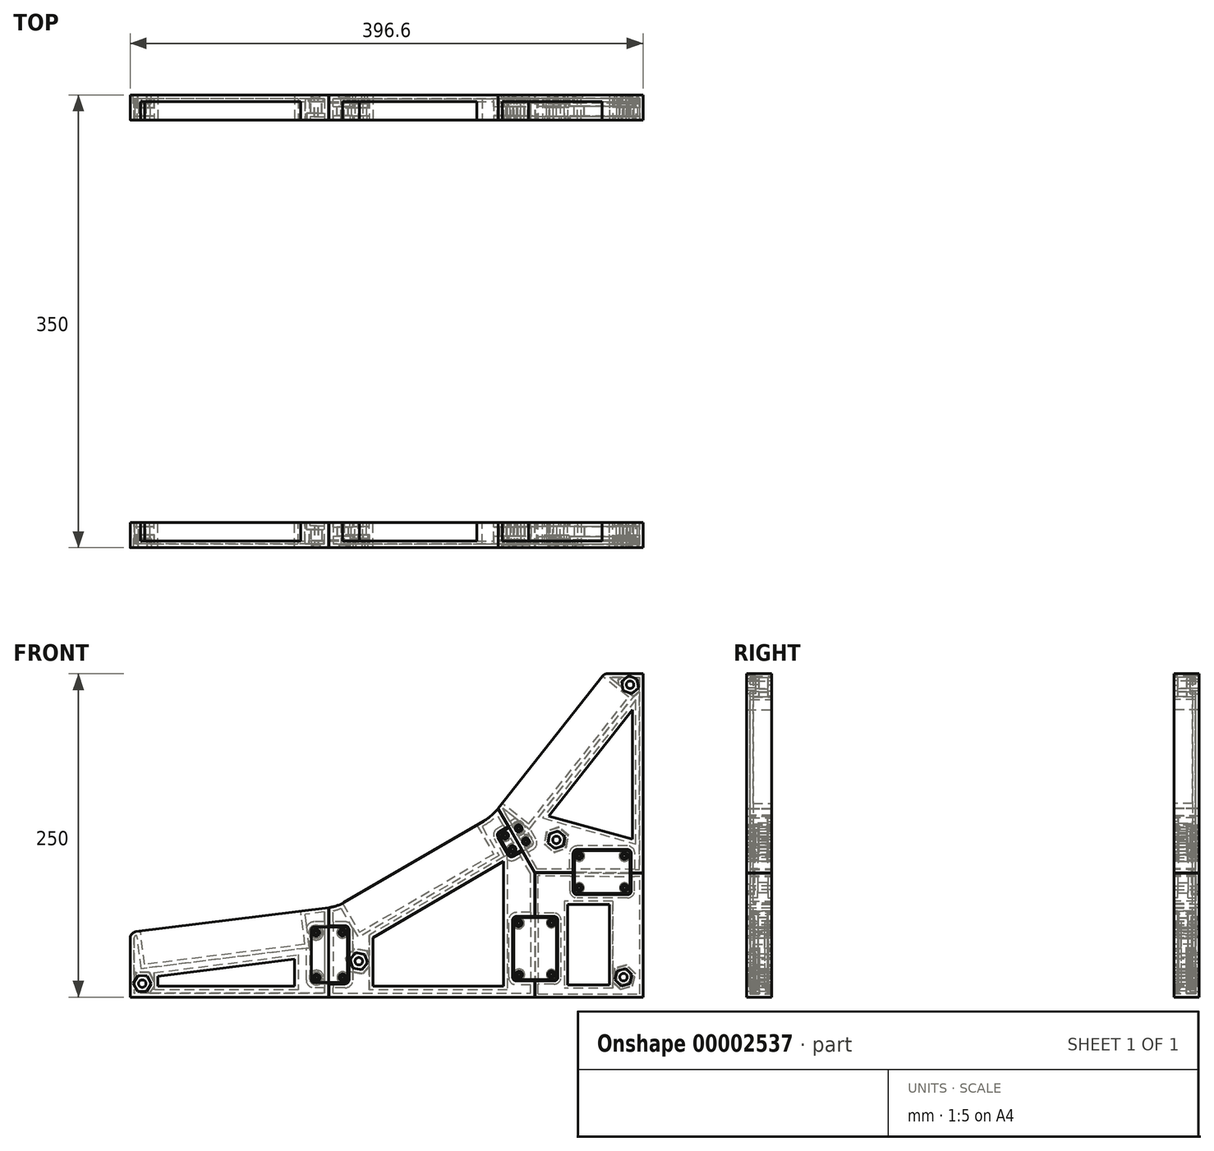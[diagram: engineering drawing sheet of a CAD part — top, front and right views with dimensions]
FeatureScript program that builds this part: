
annotation { "Feature Type Name" : "Feature", "Feature Type Description" : "" }
export const myFeature = defineFeature(function(context is Context, id is Id, definition is map)
    precondition{}
    {
        {
            var Q0;
            Q0=qCreatedBy(makeId("Front.planeOp"),FACE);
            var sketch = newSketch(context, id + "F0", { "sketchPlane" : qUnion([Q0])});
            skLineSegment(sketch, "E0", {"start": v(-139.2, -96.22) * mm, "end": v(-139.2, -46.22) * mm});
            skLineSegment(sketch, "E1", {"start": v(-139.2, -46.22) * mm, "end": v(20.8, -26.22) * mm});
            skLineSegment(sketch, "E2", {"start": v(20.8, -26.22) * mm, "end": v(140.8, 43.78) * mm});
            skLineSegment(sketch, "E3", {"start": v(140.8, 43.78) * mm, "end": v(227.4, 153.78) * mm});
            skLineSegment(sketch, "E4", {"start": v(227.4, 153.78) * mm, "end": v(257.4, 153.78) * mm});
            skLineSegment(sketch, "E5", {"start": v(257.4, 153.78) * mm, "end": v(257.4, -96.22) * mm});
            skLineSegment(sketch, "E6", {"start": v(257.4, -96.22) * mm, "end": v(-139.2, -96.22) * mm});
            skLineSegment(sketch, "E7", {"start": v(20.8, -26.22) * mm, "end": v(20.8, -96.22) * mm});
            skLineSegment(sketch, "E8", {"start": v(140.8, 43.78) * mm, "end": v(140.8, -96.22) * mm});
            skSolve(sketch);
        }
        {
            var Q0;
            {var subQ2=sQuery(id+"F0.wireOp",EDGE,"E0");Q0=makeQuery(id+"F0.imprint","IMPRINT",FACE,{"disambiguationData":[TD([[makeQuery(id+"F0.imprint","IMPRINT",EDGE,{"derivedFrom":subQ2}),-1.0]])]});}
            var Q1;
            Q1=makeQuery(id+"F0.imprint","IMPRINT",FACE,{"disambiguationData":[TD([[makeQuery(id+"F0.imprint","IMPRINT",EDGE,{"derivedFrom":sQuery(id+"F0.wireOp",EDGE,"E2")}),-1.0]])]});
            var Q2;
            Q2=makeQuery(id+"F0.imprint","IMPRINT",FACE,{"disambiguationData":[TD([[makeQuery(id+"F0.imprint","IMPRINT",EDGE,{"derivedFrom":sQuery(id+"F0.wireOp",EDGE,"E3")}),-1.0]])]});
            extrude(context, id + "F1", {"entities" : qUnion([Q0, Q1, Q2]), "oppositeDirection" : true, "depth" : 25 * mm});
        }
        {
            var Q0;
            Q0=makeQuery(id+"F1.opExtrude","CAP_FACE",FACE,{"disambiguationData":[OSD([sQuery(id+"F0.wireOp",EDGE,"E0"),sQuery(id+"F0.wireOp",EDGE,"E1"),sQuery(id+"F0.wireOp",EDGE,"E2"),sQuery(id+"F0.wireOp",EDGE,"E3"),sQuery(id+"F0.wireOp",EDGE,"E4"),sQuery(id+"F0.wireOp",EDGE,"E5"),sQuery(id+"F0.wireOp",EDGE,"E6")])],"isStart":true});
            var sketch = newSketch(context, id + "F2", { "sketchPlane" : qUnion([Q0])});
            skLineSegment(sketch, "E9.bottom", {"start": v(-131.26, -45.23) * mm, "end": v(-7.23, -29.73) * mm});
            skLineSegment(sketch, "E9.top", {"start": v(-128.04, -71.03) * mm, "end": v(-4, -55.53) * mm});
            skLineSegment(sketch, "E9.left", {"start": v(-131.26, -45.23) * mm, "end": v(-128.04, -71.03) * mm});
            skLineSegment(sketch, "E9.right", {"start": v(-7.23, -29.73) * mm, "end": v(-4, -55.53) * mm});
            skLineSegment(sketch, "E10.bottom", {"start": v(38.22, -46.16) * mm, "end": v(141.87, 14.3) * mm});
            skLineSegment(sketch, "E10.top", {"start": v(25.12, -23.7) * mm, "end": v(128.77, 36.76) * mm});
            skLineSegment(sketch, "E10.left", {"start": v(38.22, -46.16) * mm, "end": v(25.12, -23.7) * mm});
            skLineSegment(sketch, "E10.right", {"start": v(141.87, 14.3) * mm, "end": v(128.77, 36.76) * mm});
            skLineSegment(sketch, "E11.bottom", {"start": v(225.85, 151.81) * mm, "end": v(148.53, 53.6) * mm});
            skLineSegment(sketch, "E11.top", {"start": v(246.28, 135.73) * mm, "end": v(168.96, 37.51) * mm});
            skLineSegment(sketch, "E11.left", {"start": v(225.85, 151.81) * mm, "end": v(246.28, 135.73) * mm});
            skLineSegment(sketch, "E11.right", {"start": v(148.53, 53.6) * mm, "end": v(168.96, 37.51) * mm});
            skSolve(sketch);
        }
        {
            var Q0;
            Q0=makeQuery(id+"F2.imprint","IMPRINT",FACE,{"disambiguationData":[TD([[makeQuery(id+"F2.imprint","IMPRINT",EDGE,{"derivedFrom":sQuery(id+"F2.wireOp",EDGE,"E9.bottom")}),-1.0]])]});
            var Q1;
            Q1=makeQuery(id+"F2.imprint","IMPRINT",FACE,{"disambiguationData":[TD([[makeQuery(id+"F2.imprint","IMPRINT",EDGE,{"derivedFrom":sQuery(id+"F2.wireOp",EDGE,"E10.bottom")}),1.0]])]});
            var Q2;
            Q2=makeQuery(id+"F2.imprint","IMPRINT",FACE,{"disambiguationData":[TD([[makeQuery(id+"F2.imprint","IMPRINT",EDGE,{"derivedFrom":sQuery(id+"F2.wireOp",EDGE,"E11.bottom")}),-1.0]])]});
            extrude(context, id + "F3", {"entities" : qUnion([Q0, Q1, Q2]), "operationType" : NewBodyOperationType.REMOVE, "oppositeDirection" : true, "depth" : 20 * mm});
        }
        {
            var Q0;
            Q0=makeQuery(id+"F1.opExtrude","SWEPT_EDGE",EDGE,{"disambiguationData":[OSD([sQuery(id+"F0.wireOp",EDGE,"E0"),sQuery(id+"F0.wireOp",EDGE,"E1")])]});
            fillet(context, id + "F4", {"entities" : qUnion([Q0]), "radius" : 5 * mm, "tangentPropagation" : true, "allowEdgeOverflow" : false});
        }
        {
            var Q0;
            Q0=makeQuery(id+"F1.opExtrude","SWEPT_EDGE",EDGE,{"disambiguationData":[OSD([sQuery(id+"F0.wireOp",EDGE,"E1"),sQuery(id+"F0.wireOp",EDGE,"E2"),sQuery(id+"F0.wireOp",EDGE,"E7")])]});
            fillet(context, id + "F5", {"entities" : qUnion([Q0]), "radius" : 30 * mm, "tangentPropagation" : true, "allowEdgeOverflow" : false});
        }
        {
            var Q0;
            Q0=makeQuery(id+"F1.opExtrude","SWEPT_EDGE",EDGE,{"disambiguationData":[OSD([sQuery(id+"F0.wireOp",EDGE,"E2"),sQuery(id+"F0.wireOp",EDGE,"E3"),sQuery(id+"F0.wireOp",EDGE,"E8")])]});
            fillet(context, id + "F6", {"entities" : qUnion([Q0]), "radius" : 40 * mm, "tangentPropagation" : true, "allowEdgeOverflow" : false});
        }
        {
            var Q0;
            Q0=makeQuery(id+"F1.opExtrude","SWEPT_EDGE",EDGE,{"disambiguationData":[OSD([sQuery(id+"F0.wireOp",EDGE,"E3"),sQuery(id+"F0.wireOp",EDGE,"E4")])]});
            fillet(context, id + "F7", {"entities" : qUnion([Q0]), "radius" : 5 * mm, "tangentPropagation" : true, "allowEdgeOverflow" : false});
        }
        {
            var Q0;
            Q0=makeQuery(id+"F1.opExtrude","CAP_FACE",FACE,{"disambiguationData":[OSD([sQuery(id+"F0.wireOp",EDGE,"E0"),sQuery(id+"F0.wireOp",EDGE,"E1"),sQuery(id+"F0.wireOp",EDGE,"E2"),sQuery(id+"F0.wireOp",EDGE,"E3"),sQuery(id+"F0.wireOp",EDGE,"E4"),sQuery(id+"F0.wireOp",EDGE,"E5"),sQuery(id+"F0.wireOp",EDGE,"E6")])],"isStart":true});
            var sketch = newSketch(context, id + "F8", { "sketchPlane" : qUnion([Q0])});
            skCircle(sketch, "E12.cCircle", {"center": v(-129.65, -85.9) * mm, "radius": 6.5 * mm, "construction": true});
            skLineSegment(sketch, "E12.0", {"start": v(-123.16, -86.26) * mm, "end": v(-126.7, -91.7) * mm});
            skLineSegment(sketch, "E12.1", {"start": v(-126.7, -91.7) * mm, "end": v(-133.2, -91.35) * mm});
            skLineSegment(sketch, "E12.2", {"start": v(-133.2, -91.35) * mm, "end": v(-136.14, -85.55) * mm});
            skLineSegment(sketch, "E12.3", {"start": v(-136.14, -85.55) * mm, "end": v(-132.58, -80.1) * mm});
            skLineSegment(sketch, "E12.4", {"start": v(-132.58, -80.1) * mm, "end": v(-126.1, -80.46) * mm});
            skLineSegment(sketch, "E12.5", {"start": v(-126.1, -80.46) * mm, "end": v(-123.16, -86.26) * mm});
            skCircle(sketch, "E13.cCircle", {"center": v(37.59, -68.48) * mm, "radius": 6.5 * mm, "construction": true});
            skLineSegment(sketch, "E13.0", {"start": v(39.87, -74.57) * mm, "end": v(33.46, -73.5) * mm});
            skLineSegment(sketch, "E13.1", {"start": v(33.46, -73.5) * mm, "end": v(31.18, -67.41) * mm});
            skLineSegment(sketch, "E13.2", {"start": v(31.18, -67.41) * mm, "end": v(35.3, -62.4) * mm});
            skLineSegment(sketch, "E13.3", {"start": v(35.3, -62.4) * mm, "end": v(41.72, -63.46) * mm});
            skLineSegment(sketch, "E13.4", {"start": v(41.72, -63.46) * mm, "end": v(44, -69.55) * mm});
            skLineSegment(sketch, "E13.5", {"start": v(44, -69.55) * mm, "end": v(39.87, -74.57) * mm});
            skCircle(sketch, "E14.cCircle", {"center": v(247.33, 145.25) * mm, "radius": 6.5 * mm, "construction": true});
            skLineSegment(sketch, "E14.0", {"start": v(242.44, 140.98) * mm, "end": v(241.18, 147.36) * mm});
            skLineSegment(sketch, "E14.1", {"start": v(241.18, 147.36) * mm, "end": v(246.08, 151.63) * mm});
            skLineSegment(sketch, "E14.2", {"start": v(246.08, 151.63) * mm, "end": v(252.23, 149.53) * mm});
            skLineSegment(sketch, "E14.3", {"start": v(252.23, 149.53) * mm, "end": v(253.48, 143.15) * mm});
            skLineSegment(sketch, "E14.4", {"start": v(253.48, 143.15) * mm, "end": v(248.59, 138.88) * mm});
            skLineSegment(sketch, "E14.5", {"start": v(248.59, 138.88) * mm, "end": v(242.44, 140.98) * mm});
            skCircle(sketch, "E15.cCircle", {"center": v(190.4, 25.35) * mm, "radius": 6.5 * mm, "construction": true});
            skLineSegment(sketch, "E15.0", {"start": v(189, 19) * mm, "end": v(184.2, 23.38) * mm});
            skLineSegment(sketch, "E15.1", {"start": v(184.2, 23.38) * mm, "end": v(185.6, 29.73) * mm});
            skLineSegment(sketch, "E15.2", {"start": v(185.6, 29.73) * mm, "end": v(191.8, 31.7) * mm});
            skLineSegment(sketch, "E15.3", {"start": v(191.8, 31.7) * mm, "end": v(196.6, 27.31) * mm});
            skLineSegment(sketch, "E15.4", {"start": v(196.6, 27.31) * mm, "end": v(195.2, 20.96) * mm});
            skLineSegment(sketch, "E15.5", {"start": v(195.2, 20.96) * mm, "end": v(189, 19) * mm});
            skCircle(sketch, "E16.cCircle", {"center": v(242.28, -80.84) * mm, "radius": 6.4 * mm, "construction": true});
            skLineSegment(sketch, "E16.0", {"start": v(243.67, -74.59) * mm, "end": v(248.39, -78.92) * mm});
            skLineSegment(sketch, "E16.1", {"start": v(248.39, -78.92) * mm, "end": v(247, -85.16) * mm});
            skLineSegment(sketch, "E16.2", {"start": v(247, -85.16) * mm, "end": v(240.89, -87.08) * mm});
            skLineSegment(sketch, "E16.3", {"start": v(240.89, -87.08) * mm, "end": v(236.18, -82.75) * mm});
            skLineSegment(sketch, "E16.4", {"start": v(236.18, -82.75) * mm, "end": v(237.57, -76.5) * mm});
            skLineSegment(sketch, "E16.5", {"start": v(237.57, -76.5) * mm, "end": v(243.67, -74.59) * mm});
            skSolve(sketch);
        }
        {
            var Q0;
            Q0=makeQuery(id+"F8.imprint","IMPRINT",FACE,{"disambiguationData":[TD([[makeQuery(id+"F8.imprint","IMPRINT",EDGE,{"derivedFrom":sQuery(id+"F8.wireOp",EDGE,"E13.0")}),-1.0]])]});
            var Q1;
            Q1=makeQuery(id+"F8.imprint","IMPRINT",FACE,{"disambiguationData":[TD([[makeQuery(id+"F8.imprint","IMPRINT",EDGE,{"derivedFrom":sQuery(id+"F8.wireOp",EDGE,"E15.0")}),-1.0]])]});
            var Q2;
            Q2=makeQuery(id+"F8.imprint","IMPRINT",FACE,{"disambiguationData":[TD([[makeQuery(id+"F8.imprint","IMPRINT",EDGE,{"derivedFrom":sQuery(id+"F8.wireOp",EDGE,"E14.0")}),-1.0]])]});
            var Q3;
            Q3=makeQuery(id+"F8.imprint","IMPRINT",FACE,{"disambiguationData":[TD([[makeQuery(id+"F8.imprint","IMPRINT",EDGE,{"derivedFrom":sQuery(id+"F8.wireOp",EDGE,"E16.0")}),-1.0]])]});
            var Q4;
            Q4=makeQuery(id+"F8.imprint","IMPRINT",FACE,{"disambiguationData":[TD([[makeQuery(id+"F8.imprint","IMPRINT",EDGE,{"derivedFrom":sQuery(id+"F8.wireOp",EDGE,"E12.0")}),-1.0]])]});
            extrude(context, id + "F9", {"entities" : qUnion([Q0, Q1, Q2, Q3, Q4]), "operationType" : NewBodyOperationType.REMOVE, "oppositeDirection" : true, "depth" : 5.7 * mm});
        }
        {
            var Q0;
            Q0=makeQuery(id+"F1.opExtrude","CAP_FACE",FACE,{"disambiguationData":[OSD([sQuery(id+"F0.wireOp",EDGE,"E0"),sQuery(id+"F0.wireOp",EDGE,"E1"),sQuery(id+"F0.wireOp",EDGE,"E2"),sQuery(id+"F0.wireOp",EDGE,"E3"),sQuery(id+"F0.wireOp",EDGE,"E4"),sQuery(id+"F0.wireOp",EDGE,"E5"),sQuery(id+"F0.wireOp",EDGE,"E6")])],"isStart":true});
            var sketch = newSketch(context, id + "F10", { "sketchPlane" : qUnion([Q0])});
            skCircle(sketch, "E17", {"center": v(190.4, 25.35) * mm, "radius": 6.5 * mm});
            skPoint(sketch, "E17.first.point", {"position": v(185.6, 29.73) * mm});
            skPoint(sketch, "E17.second.point", {"position": v(189, 19) * mm});
            skPoint(sketch, "E17.third.point", {"position": v(196.6, 27.31) * mm});
            skCircle(sketch, "E18", {"center": v(190.4, 25.35) * mm, "radius": 2.9 * mm});
            skCircle(sketch, "E19", {"center": v(242.28, -80.84) * mm, "radius": 6.4 * mm});
            skPoint(sketch, "E19.first.point", {"position": v(236.18, -82.75) * mm});
            skPoint(sketch, "E19.second.point", {"position": v(243.67, -74.59) * mm});
            skPoint(sketch, "E19.third.point", {"position": v(247, -85.16) * mm});
            skCircle(sketch, "E20", {"center": v(37.59, -68.48) * mm, "radius": 6.5 * mm});
            skPoint(sketch, "E20.first.point", {"position": v(35.3, -62.4) * mm});
            skPoint(sketch, "E20.second.point", {"position": v(33.46, -73.5) * mm});
            skPoint(sketch, "E20.third.point", {"position": v(44, -69.55) * mm});
            skCircle(sketch, "E21", {"center": v(-129.83, -85.79) * mm, "radius": 6.32 * mm});
            skPoint(sketch, "E21.first.point", {"position": v(-136.14, -85.55) * mm});
            skPoint(sketch, "E21.second.point", {"position": v(-123.51, -85.55) * mm});
            skPoint(sketch, "E21.third.point", {"position": v(-132.58, -80.1) * mm});
            skCircle(sketch, "E22", {"center": v(-129.83, -85.79) * mm, "radius": 2.9 * mm});
            skCircle(sketch, "E23", {"center": v(37.59, -68.48) * mm, "radius": 2.9 * mm});
            skCircle(sketch, "E24", {"center": v(242.28, -80.84) * mm, "radius": 2.9 * mm});
            skCircle(sketch, "E25", {"center": v(247.33, 145.25) * mm, "radius": 6.5 * mm});
            skPoint(sketch, "E25.first.point", {"position": v(246.08, 151.63) * mm});
            skPoint(sketch, "E25.second.point", {"position": v(248.59, 138.88) * mm});
            skPoint(sketch, "E25.third.point", {"position": v(253.48, 143.15) * mm});
            skCircle(sketch, "E26", {"center": v(247.33, 145.25) * mm, "radius": 2.9 * mm});
            skSolve(sketch);
        }
        {
            var Q0;
            Q0=makeQuery(id+"F10.imprint","IMPRINT",FACE,{"disambiguationData":[TD([[makeQuery(id+"F10.imprint","IMPRINT",EDGE,{"derivedFrom":sQuery(id+"F10.wireOp",EDGE,"E18")}),1.0]])]});
            var Q1;
            Q1=makeQuery(id+"F10.imprint","IMPRINT",FACE,{"disambiguationData":[TD([[makeQuery(id+"F10.imprint","IMPRINT",EDGE,{"derivedFrom":sQuery(id+"F10.wireOp",EDGE,"E26")}),1.0]])]});
            var Q2;
            Q2=makeQuery(id+"F10.imprint","IMPRINT",FACE,{"disambiguationData":[TD([[makeQuery(id+"F10.imprint","IMPRINT",EDGE,{"derivedFrom":sQuery(id+"F10.wireOp",EDGE,"E24")}),1.0]])]});
            var Q3;
            Q3=makeQuery(id+"F10.imprint","IMPRINT",FACE,{"disambiguationData":[TD([[makeQuery(id+"F10.imprint","IMPRINT",EDGE,{"derivedFrom":sQuery(id+"F10.wireOp",EDGE,"E23")}),1.0]])]});
            var Q4;
            Q4=makeQuery(id+"F10.imprint","IMPRINT",FACE,{"disambiguationData":[TD([[makeQuery(id+"F10.imprint","IMPRINT",EDGE,{"derivedFrom":sQuery(id+"F10.wireOp",EDGE,"E22")}),1.0]])]});
            var Q5;
            Q5=sQuery(id+"F10.wireOp",EDGE,"E23");
            var Q6;
            Q6=sQuery(id+"F10.wireOp",EDGE,"E24");
            var Q7;
            Q7=sQuery(id+"F10.wireOp",EDGE,"E18");
            var Q8;
            Q8=sQuery(id+"F10.wireOp",EDGE,"E22");
            var Q9;
            Q9=sQuery(id+"F10.wireOp",EDGE,"E26");
            extrude(context, id + "F11", {"entities" : qUnion([Q0, Q1, Q2, Q3, Q4]), "operationType" : NewBodyOperationType.REMOVE, "surfaceEntities" : qUnion([Q5, Q6, Q7, Q8, Q9]), "endBound" : BoundingType.THROUGH_ALL, "oppositeDirection" : true, "depth" : 25 * mm});
        }
        {
            var Q0;
            Q0=makeQuery(id+"F1.opExtrude","CAP_FACE",FACE,{"disambiguationData":[OSD([sQuery(id+"F0.wireOp",EDGE,"E0"),sQuery(id+"F0.wireOp",EDGE,"E1"),sQuery(id+"F0.wireOp",EDGE,"E2"),sQuery(id+"F0.wireOp",EDGE,"E3"),sQuery(id+"F0.wireOp",EDGE,"E4"),sQuery(id+"F0.wireOp",EDGE,"E5"),sQuery(id+"F0.wireOp",EDGE,"E6")])],"isStart":true});
            var sketch = newSketch(context, id + "F12", { "sketchPlane" : qUnion([Q0])});
            skLineSegment(sketch, "E27", {"start": v(18.92, -24.35) * mm, "end": v(18.92, -114.52) * mm});
            skSolve(sketch);
        }
        {
            var Q0;
            Q0=sQuery(id+"F12.wireOp",EDGE,"E27");
            extrude(context, id + "F13", {"bodyType" : ToolBodyType.SURFACE, "surfaceEntities" : qUnion([Q0]), "oppositeDirection" : true, "depth" : 35 * mm});
        }
        {
            var Q0;
            Q0=makeQuery(id+"F13.opExtrude","SWEPT_BODY",BODY,{"disambiguationData":[OSD([sQuery(id+"F12.wireOp",EDGE,"E27")])]});
            deleteBodies(context, id + "F14", {"entities" : qUnion([Q0])});
        }
        {
            var Q0;
            Q0=makeQuery(id+"F1.opExtrude","CAP_FACE",FACE,{"disambiguationData":[OSD([sQuery(id+"F0.wireOp",EDGE,"E0"),sQuery(id+"F0.wireOp",EDGE,"E1"),sQuery(id+"F0.wireOp",EDGE,"E2"),sQuery(id+"F0.wireOp",EDGE,"E3"),sQuery(id+"F0.wireOp",EDGE,"E4"),sQuery(id+"F0.wireOp",EDGE,"E5"),sQuery(id+"F0.wireOp",EDGE,"E6")])],"isStart":true});
            var sketch = newSketch(context, id + "F15", { "sketchPlane" : qUnion([Q0])});
            skLineSegment(sketch, "E28.bottom", {"start": v(3, -41.04) * mm, "end": v(27, -41.04) * mm});
            skLineSegment(sketch, "E28.top", {"start": v(3, -86.04) * mm, "end": v(27, -86.04) * mm});
            skLineSegment(sketch, "E28.left", {"start": v(0, -44.04) * mm, "end": v(0, -83.04) * mm});
            skLineSegment(sketch, "E28.right", {"start": v(30, -44.04) * mm, "end": v(30, -83.04) * mm});
            skLineSegment(sketch, "E29.bottom", {"start": v(159.52, -33.77) * mm, "end": v(188.52, -33.77) * mm});
            skLineSegment(sketch, "E29.top", {"start": v(159.52, -83.77) * mm, "end": v(188.52, -83.77) * mm});
            skLineSegment(sketch, "E29.left", {"start": v(156.52, -36.77) * mm, "end": v(156.52, -80.77) * mm});
            skLineSegment(sketch, "E29.right", {"start": v(191.52, -36.77) * mm, "end": v(191.52, -80.77) * mm});
            skLineSegment(sketch, "E30.bottom", {"start": v(206.31, 17.9) * mm, "end": v(245.31, 17.9) * mm});
            skLineSegment(sketch, "E30.top", {"start": v(206.31, -17.1) * mm, "end": v(245.31, -17.1) * mm});
            skLineSegment(sketch, "E30.left", {"start": v(203.31, 14.9) * mm, "end": v(203.31, -14.1) * mm});
            skLineSegment(sketch, "E30.right", {"start": v(248.31, 14.9) * mm, "end": v(248.31, -14.1) * mm});
            skLineSegment(sketch, "E31", {"start": v(145.5, 49.75) * mm, "end": v(173.66, 0.3) * mm});
            skLineSegment(sketch, "E32", {"start": v(173.83, 0) * mm, "end": v(257.4, -0.54) * mm});
            skLineSegment(sketch, "E33", {"start": v(255.56, -0.53) * mm, "end": v(173.83, 0) * mm});
            skLineSegment(sketch, "E34", {"start": v(173.83, 0) * mm, "end": v(173.83, -96.22) * mm});
            skLineSegment(sketch, "E35", {"start": v(14.7, -26.99) * mm, "end": v(14.7, -96.22) * mm});
            skLineSegment(sketch, "E36.0", {"start": v(14.2, -26.99) * mm, "end": v(14.2, -96.22) * mm});
            skLineSegment(sketch, "E37", {"start": v(14.2, -26.99) * mm, "end": v(14.7, -26.99) * mm});
            skLineSegment(sketch, "E38", {"start": v(17.21, -22.5) * mm, "end": v(25.96, -10.57) * mm});
            skLineSegment(sketch, "E39", {"start": v(14.2, -96.22) * mm, "end": v(14.7, -96.22) * mm});
            skLineSegment(sketch, "E40.0", {"start": v(173.53, -0.08) * mm, "end": v(173.53, -96.22) * mm});
            skLineSegment(sketch, "E40.1", {"start": v(145.24, 49.6) * mm, "end": v(173.53, -0.08) * mm});
            skLineSegment(sketch, "E41", {"start": v(145.24, 49.6) * mm, "end": v(145.5, 49.75) * mm});
            skLineSegment(sketch, "E42", {"start": v(173.53, -96.22) * mm, "end": v(173.83, -96.22) * mm});
            skLineSegment(sketch, "E43.0", {"start": v(257.4, -0.24) * mm, "end": v(173.66, 0.3) * mm});
            skLineSegment(sketch, "E44", {"start": v(257.4, -0.87) * mm, "end": v(257.4, -1.3) * mm});
            skLineSegment(sketch, "E45", {"start": v(257.4, -0.24) * mm, "end": v(257.4, -0.54) * mm});
            skLineSegment(sketch, "E46", {"start": v(146.3, 31.68) * mm, "end": v(160.2, 39.6) * mm});
            skLineSegment(sketch, "E47", {"start": v(164.29, 38.47) * mm, "end": v(172.2, 24.57) * mm});
            skLineSegment(sketch, "E48", {"start": v(171.08, 20.48) * mm, "end": v(157.18, 12.56) * mm});
            skLineSegment(sketch, "E49", {"start": v(145.17, 27.59) * mm, "end": v(153.09, 13.68) * mm});
            skPoint(sketch, "E50.visualSharp", {"position": v(143.69, 30.2) * mm});
            skArc(sketch, "E50.filletArc", {"start": v(146.3, 31.68) * mm, "mid": v(144.88, 29.86) * mm, "end": v(145.17, 27.59) * mm});
            skPoint(sketch, "E51.visualSharp", {"position": v(162.8, 41.08) * mm});
            skArc(sketch, "E51.filletArc", {"start": v(164.29, 38.47) * mm, "mid": v(162.47, 39.88) * mm, "end": v(160.2, 39.6) * mm});
            skPoint(sketch, "E52.visualSharp", {"position": v(173.7, 21.96) * mm});
            skArc(sketch, "E52.filletArc", {"start": v(171.08, 20.48) * mm, "mid": v(172.5, 22.29) * mm, "end": v(172.2, 24.57) * mm});
            skPoint(sketch, "E53.visualSharp", {"position": v(154.57, 11.07) * mm});
            skArc(sketch, "E53.filletArc", {"start": v(153.09, 13.68) * mm, "mid": v(154.9, 12.27) * mm, "end": v(157.18, 12.56) * mm});
            skPoint(sketch, "E54.visualSharp", {"position": v(156.52, -33.77) * mm});
            skArc(sketch, "E54.filletArc", {"start": v(159.52, -33.77) * mm, "mid": v(157.4, -34.65) * mm, "end": v(156.52, -36.77) * mm});
            skPoint(sketch, "E55.visualSharp", {"position": v(191.52, -33.77) * mm});
            skArc(sketch, "E55.filletArc", {"start": v(191.52, -36.77) * mm, "mid": v(190.64, -34.65) * mm, "end": v(188.52, -33.77) * mm});
            skPoint(sketch, "E56.visualSharp", {"position": v(203.31, -17.1) * mm});
            skArc(sketch, "E56.filletArc", {"start": v(203.31, -14.1) * mm, "mid": v(204.2, -16.21) * mm, "end": v(206.31, -17.1) * mm});
            skPoint(sketch, "E57.visualSharp", {"position": v(203.31, 17.9) * mm});
            skArc(sketch, "E57.filletArc", {"start": v(206.31, 17.9) * mm, "mid": v(204.2, 17.03) * mm, "end": v(203.31, 14.9) * mm});
            skPoint(sketch, "E58.visualSharp", {"position": v(248.31, 17.9) * mm});
            skArc(sketch, "E58.filletArc", {"start": v(248.31, 14.9) * mm, "mid": v(247.43, 17.03) * mm, "end": v(245.31, 17.9) * mm});
            skPoint(sketch, "E59.visualSharp", {"position": v(248.31, -17.1) * mm});
            skArc(sketch, "E59.filletArc", {"start": v(245.31, -17.1) * mm, "mid": v(247.43, -16.21) * mm, "end": v(248.31, -14.1) * mm});
            skPoint(sketch, "E60.visualSharp", {"position": v(156.52, -83.77) * mm});
            skArc(sketch, "E60.filletArc", {"start": v(156.52, -80.77) * mm, "mid": v(157.4, -82.9) * mm, "end": v(159.52, -83.77) * mm});
            skPoint(sketch, "E61.visualSharp", {"position": v(191.52, -83.77) * mm});
            skArc(sketch, "E61.filletArc", {"start": v(188.52, -83.77) * mm, "mid": v(190.64, -82.9) * mm, "end": v(191.52, -80.77) * mm});
            skPoint(sketch, "E62.visualSharp", {"position": v(0, -41.04) * mm});
            skArc(sketch, "E62.filletArc", {"start": v(3, -41.04) * mm, "mid": v(0.88, -41.92) * mm, "end": v(0, -44.04) * mm});
            skPoint(sketch, "E63.visualSharp", {"position": v(30, -41.04) * mm});
            skArc(sketch, "E63.filletArc", {"start": v(30, -44.04) * mm, "mid": v(29.12, -41.92) * mm, "end": v(27, -41.04) * mm});
            skPoint(sketch, "E64.visualSharp", {"position": v(0, -86.04) * mm});
            skArc(sketch, "E64.filletArc", {"start": v(0, -83.04) * mm, "mid": v(0.88, -85.16) * mm, "end": v(3, -86.04) * mm});
            skPoint(sketch, "E65.visualSharp", {"position": v(30, -86.04) * mm});
            skArc(sketch, "E65.filletArc", {"start": v(27, -86.04) * mm, "mid": v(29.12, -85.16) * mm, "end": v(30, -83.04) * mm});
            skSolve(sketch);
        }
        {
            var Q0;
            {var subQ0=sQuery(id+"F15.wireOp",EDGE,"E39");Q0=makeQuery(id+"F15.imprint","IMPRINT",FACE,{"disambiguationData":[TD([[makeQuery(id+"F15.imprint","IMPRINT",EDGE,{"derivedFrom":subQ0}),-1.0]])]});}
            var Q1;
            {var subQ3=sQuery(id+"F15.wireOp",EDGE,"E28.bottom");var subQ5=sQuery(id+"F15.wireOp",EDGE,"E36.0");var subQ7=makeQuery(id+"F15.imprint","INTERSECT",VERTEX,{"derivedFrom":[subQ3,subQ5]});Q1=makeQuery(id+"F15.imprint","IMPRINT",FACE,{"disambiguationData":[TD([[makeQuery(id+"F15.imprint","IMPRINT",EDGE,{"disambiguationData":[TD([[subQ7,-1.0]])],"derivedFrom":subQ3}),-1.0]])]});}
            var Q2;
            {var subQ4=sQuery(id+"F15.wireOp",EDGE,"E36.0");var subQ8=sQuery(id+"F15.wireOp",EDGE,"E28.bottom");var subQ9=makeQuery(id+"F15.imprint","INTERSECT",VERTEX,{"derivedFrom":[subQ8,subQ4]});Q2=makeQuery(id+"F15.imprint","IMPRINT",FACE,{"disambiguationData":[TD([[makeQuery(id+"F15.imprint","IMPRINT",EDGE,{"disambiguationData":[TD([[subQ9,-1.0]])],"derivedFrom":subQ8}),1.0]])]});}
            extrude(context, id + "F16", {"entities" : qUnion([Q0, Q1, Q2]), "operationType" : NewBodyOperationType.REMOVE, "oppositeDirection" : true, "depth" : 25 * mm});
        }
        {
            var Q0;
            {var subQ6=sQuery(id+"F15.wireOp",EDGE,"E32");Q0=makeQuery(id+"F15.imprint","IMPRINT",FACE,{"disambiguationData":[TD([[makeQuery(id+"F15.imprint","IMPRINT",EDGE,{"derivedFrom":subQ6}),1.0]])]});}
            var Q1;
            {var subQ6=sQuery(id+"F15.wireOp",EDGE,"E31");Q1=makeQuery(id+"F15.imprint","IMPRINT",FACE,{"disambiguationData":[TD([[makeQuery(id+"F15.imprint","IMPRINT",EDGE,{"derivedFrom":subQ6}),-1.0]])]});}
            var Q2;
            {var subQ0=sQuery(id+"F15.wireOp",EDGE,"E43.0");var subQ3=sQuery(id+"F15.wireOp",EDGE,"E30.left");var subQ4=makeQuery(id+"F15.imprint","INTERSECT",VERTEX,{"derivedFrom":[subQ3,subQ0]});Q2=makeQuery(id+"F15.imprint","IMPRINT",FACE,{"disambiguationData":[TD([[makeQuery(id+"F15.imprint","IMPRINT",EDGE,{"disambiguationData":[TD([[subQ4,-1.0]])],"derivedFrom":subQ3}),1.0]])]});}
            var Q3;
            {var subQ0=sQuery(id+"F15.wireOp",EDGE,"E42");Q3=makeQuery(id+"F15.imprint","IMPRINT",FACE,{"disambiguationData":[TD([[makeQuery(id+"F15.imprint","IMPRINT",EDGE,{"derivedFrom":subQ0}),-1.0]])]});}
            var Q4;
            {var subQ0=sQuery(id+"F15.wireOp",EDGE,"E40.0");var subQ3=sQuery(id+"F15.wireOp",EDGE,"E29.bottom");var subQ4=makeQuery(id+"F15.imprint","INTERSECT",VERTEX,{"derivedFrom":[subQ3,subQ0]});Q4=makeQuery(id+"F15.imprint","IMPRINT",FACE,{"disambiguationData":[TD([[makeQuery(id+"F15.imprint","IMPRINT",EDGE,{"disambiguationData":[TD([[subQ4,-1.0]])],"derivedFrom":subQ3}),-1.0]])]});}
            var Q5;
            {var subQ9=sQuery(id+"F15.wireOp",EDGE,"E40.0");var subQ10=sQuery(id+"F15.wireOp",EDGE,"E29.bottom");var subQ11=makeQuery(id+"F15.imprint","INTERSECT",VERTEX,{"derivedFrom":[subQ10,subQ9]});Q5=makeQuery(id+"F15.imprint","IMPRINT",FACE,{"disambiguationData":[TD([[makeQuery(id+"F15.imprint","IMPRINT",EDGE,{"disambiguationData":[TD([[subQ11,-1.0]])],"derivedFrom":subQ10}),1.0]])]});}
            var Q6;
            {var subQ6=sQuery(id+"F15.wireOp",EDGE,"E31");var subQ8=sQuery(id+"F15.wireOp",EDGE,"E46");var subQ10=makeQuery(id+"F15.imprint","INTERSECT",VERTEX,{"derivedFrom":[subQ6,subQ8]});Q6=makeQuery(id+"F15.imprint","IMPRINT",FACE,{"disambiguationData":[TD([[makeQuery(id+"F15.imprint","IMPRINT",EDGE,{"disambiguationData":[TD([[subQ10,1.0]])],"derivedFrom":subQ8}),1.0]])]});}
            extrude(context, id + "F17", {"entities" : qUnion([Q0, Q1, Q2, Q3, Q4, Q5, Q6]), "operationType" : NewBodyOperationType.REMOVE, "oppositeDirection" : true, "depth" : 30 * mm});
        }
        {
            var Q0;
            Q0=makeQuery(id+"F15.imprint","IMPRINT",FACE,{"disambiguationData":[TD([[makeQuery(id+"F15.imprint","IMPRINT",EDGE,{"derivedFrom":sQuery(id+"F15.wireOp",EDGE,"E28.left")}),1.0]])]});
            extrude(context, id + "F18", {"entities" : qUnion([Q0]), "operationType" : NewBodyOperationType.REMOVE, "oppositeDirection" : true, "depth" : 8 * mm});
        }
        {
            var Q0;
            Q0=makeQuery(id+"F15.imprint","IMPRINT",FACE,{"disambiguationData":[TD([[makeQuery(id+"F15.imprint","IMPRINT",EDGE,{"derivedFrom":sQuery(id+"F15.wireOp",EDGE,"E28.right")}),-1.0]])]});
            extrude(context, id + "F19", {"entities" : qUnion([Q0]), "operationType" : NewBodyOperationType.REMOVE, "oppositeDirection" : true, "depth" : 6 * mm});
        }
        {
            var Q0;
            {var subQ0=sQuery(id+"F0.wireOp",EDGE,"E1");var subQ1=sQuery(id+"F0.wireOp",EDGE,"E2");var subQ2=sQuery(id+"F0.wireOp",EDGE,"E3");var subQ3=sQuery(id+"F0.wireOp",EDGE,"E4");var subQ4=sQuery(id+"F0.wireOp",EDGE,"E5");var subQ5=sQuery(id+"F0.wireOp",EDGE,"E6");var subQ8=makeQuery(id+"F11.boolean.opBoolean","COPY",FACE,{"derivedFrom":makeQuery(id+"F11.opExtrude","SWEPT_FACE",FACE,{"disambiguationData":[OSD([sQuery(id+"F10.wireOp",EDGE,"E24")])]})});var subQ17=makeQuery(id+"F1.opExtrude","SWEPT_FACE",FACE,{"disambiguationData":[OSD([subQ2])]});var subQ18=makeQuery(id+"F1.opExtrude","SWEPT_FACE",FACE,{"disambiguationData":[OSD([subQ1])]});var subQ19=makeQuery(id+"F16.boolean.opBoolean","SPLIT",FACE,{"disambiguationData":[TD([subQ18])],"derivedFrom":makeQuery(id+"F1.opExtrude","CAP_FACE",FACE,{"disambiguationData":[OSD([sQuery(id+"F0.wireOp",EDGE,"E0"),subQ0,subQ1,subQ2,subQ3,subQ4,subQ5])],"isStart":false})});Q0=qUnion([makeQuery(id+"F17.boolean.opBoolean","SPLIT",FACE,{"disambiguationData":[TD([subQ18])],"derivedFrom":subQ19}),makeQuery(id+"F17.boolean.opBoolean","SPLIT",FACE,{"disambiguationData":[TD([subQ17])],"derivedFrom":subQ19}),makeQuery(id+"F17.boolean.opBoolean","SPLIT",FACE,{"disambiguationData":[TD([subQ8])],"derivedFrom":subQ19})]);}
            var sketch = newSketch(context, id + "F20", { "sketchPlane" : qUnion([Q0])});
            skLineSegment(sketch, "E66.0", {"start": v(-206.31, 17.9) * mm, "end": v(-245.31, 17.9) * mm});
            skArc(sketch, "E67.0", {"start": v(-206.31, 17.9) * mm, "mid": v(-204.2, 17.03) * mm, "end": v(-203.31, 14.9) * mm});
            skLineSegment(sketch, "E68.0", {"start": v(-203.31, 14.9) * mm, "end": v(-203.31, -14.1) * mm});
            skLineSegment(sketch, "E69.0", {"start": v(-206.31, -17.1) * mm, "end": v(-245.31, -17.1) * mm});
            skArc(sketch, "E70.0", {"start": v(-203.31, -14.1) * mm, "mid": v(-204.2, -16.21) * mm, "end": v(-206.31, -17.1) * mm});
            skLineSegment(sketch, "E71.0", {"start": v(-248.31, 14.9) * mm, "end": v(-248.31, -14.1) * mm});
            skArc(sketch, "E72.0", {"start": v(-248.31, 14.9) * mm, "mid": v(-247.43, 17.03) * mm, "end": v(-245.31, 17.9) * mm});
            skArc(sketch, "E73.0", {"start": v(-245.31, -17.1) * mm, "mid": v(-247.43, -16.21) * mm, "end": v(-248.31, -14.1) * mm});
            skLineSegment(sketch, "E74.0", {"start": v(-145.17, 27.59) * mm, "end": v(-153.09, 13.68) * mm});
            skArc(sketch, "E75.0", {"start": v(-146.3, 31.68) * mm, "mid": v(-144.88, 29.86) * mm, "end": v(-145.17, 27.59) * mm});
            skLineSegment(sketch, "E76.0", {"start": v(-146.3, 31.68) * mm, "end": v(-160.2, 39.6) * mm});
            skArc(sketch, "E77.0", {"start": v(-164.29, 38.47) * mm, "mid": v(-162.47, 39.88) * mm, "end": v(-160.2, 39.6) * mm});
            skLineSegment(sketch, "E78.0", {"start": v(-164.29, 38.47) * mm, "end": v(-172.2, 24.57) * mm});
            skLineSegment(sketch, "E79.0", {"start": v(-171.08, 20.48) * mm, "end": v(-157.18, 12.56) * mm});
            skArc(sketch, "E80.0", {"start": v(-153.09, 13.68) * mm, "mid": v(-154.9, 12.27) * mm, "end": v(-157.18, 12.56) * mm});
            skArc(sketch, "E81.0", {"start": v(-171.08, 20.48) * mm, "mid": v(-172.5, 22.29) * mm, "end": v(-172.2, 24.57) * mm});
            skLineSegment(sketch, "E82.0", {"start": v(-159.52, -33.77) * mm, "end": v(-188.52, -33.77) * mm});
            skArc(sketch, "E83.0", {"start": v(-191.52, -36.77) * mm, "mid": v(-190.64, -34.65) * mm, "end": v(-188.52, -33.77) * mm});
            skLineSegment(sketch, "E84.0", {"start": v(-191.52, -36.77) * mm, "end": v(-191.52, -80.77) * mm});
            skArc(sketch, "E85.0", {"start": v(-188.52, -83.77) * mm, "mid": v(-190.64, -82.9) * mm, "end": v(-191.52, -80.77) * mm});
            skLineSegment(sketch, "E86.0", {"start": v(-159.52, -83.77) * mm, "end": v(-188.52, -83.77) * mm});
            skLineSegment(sketch, "E87.0", {"start": v(-156.52, -36.77) * mm, "end": v(-156.52, -80.77) * mm});
            skArc(sketch, "E88.0", {"start": v(-156.52, -80.77) * mm, "mid": v(-157.4, -82.9) * mm, "end": v(-159.52, -83.77) * mm});
            skArc(sketch, "E89.0", {"start": v(-159.52, -33.77) * mm, "mid": v(-157.4, -34.65) * mm, "end": v(-156.52, -36.77) * mm});
            skLineSegment(sketch, "E90.0", {"start": v(-30, -44.04) * mm, "end": v(-30, -83.04) * mm});
            skLineSegment(sketch, "E91.0", {"start": v(-3, -41.04) * mm, "end": v(-27, -41.04) * mm});
            skArc(sketch, "E92.0", {"start": v(-30, -44.04) * mm, "mid": v(-29.12, -41.92) * mm, "end": v(-27, -41.04) * mm});
            skArc(sketch, "E93.0", {"start": v(-3, -41.04) * mm, "mid": v(-0.88, -41.92) * mm, "end": v(0, -44.04) * mm});
            skLineSegment(sketch, "E94.0", {"start": v(0, -44.04) * mm, "end": v(0, -83.04) * mm});
            skLineSegment(sketch, "E95.0", {"start": v(-3, -86.04) * mm, "end": v(-27, -86.04) * mm});
            skArc(sketch, "E96.0", {"start": v(0, -83.04) * mm, "mid": v(-0.88, -85.16) * mm, "end": v(-3, -86.04) * mm});
            skArc(sketch, "E97.0", {"start": v(-27, -86.04) * mm, "mid": v(-29.12, -85.16) * mm, "end": v(-30, -83.04) * mm});
            skSolve(sketch);
        }
        {
            var Q0;
            Q0=makeQuery(id+"F15.imprint","IMPRINT",FACE,{"disambiguationData":[TD([[makeQuery(id+"F15.imprint","IMPRINT",EDGE,{"derivedFrom":sQuery(id+"F15.wireOp",EDGE,"E30.bottom")}),-1.0]])]});
            var Q1;
            Q1=makeQuery(id+"F15.imprint","IMPRINT",FACE,{"disambiguationData":[TD([[makeQuery(id+"F15.imprint","IMPRINT",EDGE,{"derivedFrom":sQuery(id+"F15.wireOp",EDGE,"E29.right")}),-1.0]])]});
            var Q2;
            Q2=makeQuery(id+"F15.imprint","IMPRINT",FACE,{"disambiguationData":[TD([[makeQuery(id+"F15.imprint","IMPRINT",EDGE,{"derivedFrom":sQuery(id+"F15.wireOp",EDGE,"E49")}),1.0]])]});
            var Q3;
            Q3=makeQuery(id+"F15.imprint","IMPRINT",FACE,{"disambiguationData":[TD([[makeQuery(id+"F15.imprint","IMPRINT",EDGE,{"derivedFrom":sQuery(id+"F15.wireOp",EDGE,"E47")}),-1.0]])]});
            var Q4;
            Q4=makeQuery(id+"F15.imprint","IMPRINT",FACE,{"disambiguationData":[TD([[makeQuery(id+"F15.imprint","IMPRINT",EDGE,{"derivedFrom":sQuery(id+"F15.wireOp",EDGE,"E29.left")}),1.0]])]});
            var Q5;
            Q5=makeQuery(id+"F15.imprint","IMPRINT",FACE,{"disambiguationData":[TD([[makeQuery(id+"F15.imprint","IMPRINT",EDGE,{"derivedFrom":sQuery(id+"F15.wireOp",EDGE,"E30.top")}),1.0]])]});
            extrude(context, id + "F21", {"entities" : qUnion([Q0, Q1, Q2, Q3, Q4, Q5]), "operationType" : NewBodyOperationType.REMOVE, "oppositeDirection" : true, "depth" : 6 * mm});
        }
        {
            var Q0;
            Q0=makeQuery(id+"F20.imprint","IMPRINT",FACE,{"disambiguationData":[TD([[makeQuery(id+"F20.imprint","IMPRINT",EDGE,{"derivedFrom":sQuery(id+"F20.wireOp",EDGE,"E74.0")}),-1.0]])]});
            var Q1;
            Q1=makeQuery(id+"F20.imprint","IMPRINT",FACE,{"disambiguationData":[TD([[makeQuery(id+"F20.imprint","IMPRINT",EDGE,{"derivedFrom":sQuery(id+"F20.wireOp",EDGE,"E82.0")}),1.0]])]});
            var Q2;
            Q2=makeQuery(id+"F20.imprint","IMPRINT",FACE,{"disambiguationData":[TD([[makeQuery(id+"F20.imprint","IMPRINT",EDGE,{"derivedFrom":sQuery(id+"F20.wireOp",EDGE,"E66.0")}),1.0]])]});
            var Q3;
            Q3=makeQuery(id+"F20.imprint","IMPRINT",FACE,{"disambiguationData":[TD([[makeQuery(id+"F20.imprint","IMPRINT",EDGE,{"derivedFrom":sQuery(id+"F20.wireOp",EDGE,"E90.0")}),1.0]])]});
            extrude(context, id + "F22", {"entities" : qUnion([Q0, Q1, Q2, Q3]), "operationType" : NewBodyOperationType.REMOVE, "oppositeDirection" : true, "depth" : 6 * mm});
        }
        {
            var Q0;
            {var subQ0=sQuery(id+"F0.wireOp",EDGE,"E1");var subQ1=sQuery(id+"F0.wireOp",EDGE,"E2");var subQ2=sQuery(id+"F0.wireOp",EDGE,"E3");var subQ3=sQuery(id+"F0.wireOp",EDGE,"E4");var subQ4=sQuery(id+"F0.wireOp",EDGE,"E5");var subQ5=sQuery(id+"F0.wireOp",EDGE,"E6");var subQ11=makeQuery(id+"F1.opExtrude","SWEPT_FACE",FACE,{"disambiguationData":[OSD([subQ2])]});Q0=makeQuery(id+"F17.boolean.opBoolean","SPLIT",FACE,{"disambiguationData":[TD([subQ11])],"derivedFrom":makeQuery(id+"F16.boolean.opBoolean","SPLIT",FACE,{"disambiguationData":[TD([makeQuery(id+"F1.opExtrude","SWEPT_FACE",FACE,{"disambiguationData":[OSD([subQ1])]})])],"derivedFrom":makeQuery(id+"F1.opExtrude","CAP_FACE",FACE,{"disambiguationData":[OSD([sQuery(id+"F0.wireOp",EDGE,"E0"),subQ0,subQ1,subQ2,subQ3,subQ4,subQ5])],"isStart":false})})});}
            var sketch = newSketch(context, id + "F23", { "sketchPlane" : qUnion([Q0])});
            skLineSegment(sketch, "E98.0", {"start": v(-206.31, 16.9) * mm, "end": v(-245.31, 16.9) * mm});
            skArc(sketch, "E98.1", {"start": v(-247.31, 14.9) * mm, "mid": v(-246.73, 16.32) * mm, "end": v(-245.31, 16.9) * mm});
            skLineSegment(sketch, "E98.2", {"start": v(-247.31, 14.9) * mm, "end": v(-247.31, -14.1) * mm});
            skArc(sketch, "E98.3", {"start": v(-245.31, -16.1) * mm, "mid": v(-246.73, -15.5) * mm, "end": v(-247.31, -14.1) * mm});
            skLineSegment(sketch, "E98.4", {"start": v(-206.31, -16.1) * mm, "end": v(-245.31, -16.1) * mm});
            skArc(sketch, "E98.5", {"start": v(-206.31, 16.9) * mm, "mid": v(-204.9, 16.32) * mm, "end": v(-204.31, 14.9) * mm});
            skArc(sketch, "E98.6", {"start": v(-204.31, -14.1) * mm, "mid": v(-204.9, -15.5) * mm, "end": v(-206.31, -16.1) * mm});
            skLineSegment(sketch, "E98.7", {"start": v(-204.31, 14.9) * mm, "end": v(-204.31, -14.1) * mm});
            skLineSegment(sketch, "E99.0", {"start": v(-146.04, 28.08) * mm, "end": v(-153.96, 14.18) * mm});
            skLineSegment(sketch, "E99.1", {"start": v(-146.79, 30.8) * mm, "end": v(-160.7, 38.73) * mm});
            skLineSegment(sketch, "E99.2", {"start": v(-163.42, 37.98) * mm, "end": v(-171.34, 24.07) * mm});
            skLineSegment(sketch, "E99.3", {"start": v(-170.59, 21.35) * mm, "end": v(-156.68, 13.43) * mm});
            skLineSegment(sketch, "E100.0", {"start": v(-159.52, -34.77) * mm, "end": v(-188.52, -34.77) * mm});
            skArc(sketch, "E100.1", {"start": v(-190.52, -36.77) * mm, "mid": v(-189.94, -35.36) * mm, "end": v(-188.52, -34.77) * mm});
            skLineSegment(sketch, "E100.2", {"start": v(-190.52, -36.77) * mm, "end": v(-190.52, -80.77) * mm});
            skArc(sketch, "E100.3", {"start": v(-188.52, -82.77) * mm, "mid": v(-189.94, -82.19) * mm, "end": v(-190.52, -80.77) * mm});
            skLineSegment(sketch, "E100.4", {"start": v(-159.52, -82.77) * mm, "end": v(-188.52, -82.77) * mm});
            skArc(sketch, "E100.5", {"start": v(-159.52, -34.77) * mm, "mid": v(-158.1, -35.36) * mm, "end": v(-157.52, -36.77) * mm});
            skArc(sketch, "E100.6", {"start": v(-157.52, -80.77) * mm, "mid": v(-158.1, -82.19) * mm, "end": v(-159.52, -82.77) * mm});
            skLineSegment(sketch, "E100.7", {"start": v(-157.52, -36.77) * mm, "end": v(-157.52, -80.77) * mm});
            skLineSegment(sketch, "E101.0", {"start": v(-29, -44.04) * mm, "end": v(-29, -83.04) * mm});
            skArc(sketch, "E101.1", {"start": v(-27, -85.04) * mm, "mid": v(-28.41, -84.45) * mm, "end": v(-29, -83.04) * mm});
            skLineSegment(sketch, "E101.2", {"start": v(-3, -85.04) * mm, "end": v(-27, -85.04) * mm});
            skArc(sketch, "E101.3", {"start": v(-1, -83.04) * mm, "mid": v(-1.59, -84.45) * mm, "end": v(-3, -85.04) * mm});
            skLineSegment(sketch, "E101.4", {"start": v(-1, -44.04) * mm, "end": v(-1, -83.04) * mm});
            skArc(sketch, "E101.5", {"start": v(-29, -44.04) * mm, "mid": v(-28.41, -42.62) * mm, "end": v(-27, -42.04) * mm});
            skArc(sketch, "E101.6", {"start": v(-3, -42.04) * mm, "mid": v(-1.59, -42.62) * mm, "end": v(-1, -44.04) * mm});
            skLineSegment(sketch, "E101.7", {"start": v(-3, -42.04) * mm, "end": v(-27, -42.04) * mm});
            skPoint(sketch, "E102.visualSharp", {"position": v(-145.05, 29.82) * mm});
            skArc(sketch, "E102.filletArc", {"start": v(-146.04, 28.08) * mm, "mid": v(-145.85, 29.6) * mm, "end": v(-146.79, 30.8) * mm});
            skPoint(sketch, "E103.visualSharp", {"position": v(-154.95, 12.44) * mm});
            skArc(sketch, "E103.filletArc", {"start": v(-156.68, 13.43) * mm, "mid": v(-155.17, 13.24) * mm, "end": v(-153.96, 14.18) * mm});
            skPoint(sketch, "E104.visualSharp", {"position": v(-172.33, 22.34) * mm});
            skArc(sketch, "E104.filletArc", {"start": v(-171.34, 24.07) * mm, "mid": v(-171.53, 22.55) * mm, "end": v(-170.59, 21.35) * mm});
            skPoint(sketch, "E105.visualSharp", {"position": v(-162.43, 39.71) * mm});
            skArc(sketch, "E105.filletArc", {"start": v(-160.7, 38.73) * mm, "mid": v(-162.21, 38.92) * mm, "end": v(-163.42, 37.98) * mm});
            skSolve(sketch);
        }
        {
            var Q0;
            Q0=makeQuery(id+"F23.imprint","IMPRINT",FACE,{"disambiguationData":[TD([[makeQuery(id+"F23.imprint","IMPRINT",EDGE,{"derivedFrom":sQuery(id+"F23.wireOp",EDGE,"E99.0")}),-1.0]])]});
            var Q1;
            Q1=makeQuery(id+"F23.imprint","IMPRINT",FACE,{"disambiguationData":[TD([[makeQuery(id+"F23.imprint","IMPRINT",EDGE,{"derivedFrom":sQuery(id+"F23.wireOp",EDGE,"E98.0")}),1.0]])]});
            var Q2;
            Q2=makeQuery(id+"F23.imprint","IMPRINT",FACE,{"disambiguationData":[TD([[makeQuery(id+"F23.imprint","IMPRINT",EDGE,{"derivedFrom":sQuery(id+"F23.wireOp",EDGE,"E100.0")}),1.0]])]});
            var Q3;
            Q3=makeQuery(id+"F23.imprint","IMPRINT",FACE,{"disambiguationData":[TD([[makeQuery(id+"F23.imprint","IMPRINT",EDGE,{"derivedFrom":sQuery(id+"F23.wireOp",EDGE,"E101.0")}),1.0]])]});
            extrude(context, id + "F24", {"entities" : qUnion([Q0, Q1, Q2, Q3]), "oppositeDirection" : true, "depth" : 5 * mm});
        }
        {
            var Q0;
            {var subQ0=sQuery(id+"F0.wireOp",EDGE,"E1");var subQ1=sQuery(id+"F0.wireOp",EDGE,"E2");var subQ2=sQuery(id+"F0.wireOp",EDGE,"E3");var subQ3=sQuery(id+"F0.wireOp",EDGE,"E4");var subQ4=sQuery(id+"F0.wireOp",EDGE,"E5");var subQ5=sQuery(id+"F0.wireOp",EDGE,"E6");var subQ11=makeQuery(id+"F1.opExtrude","SWEPT_FACE",FACE,{"disambiguationData":[OSD([subQ1])]});Q0=makeQuery(id+"F17.boolean.opBoolean","SPLIT",FACE,{"disambiguationData":[TD([subQ11])],"derivedFrom":makeQuery(id+"F16.boolean.opBoolean","SPLIT",FACE,{"disambiguationData":[TD([subQ11])],"derivedFrom":makeQuery(id+"F1.opExtrude","CAP_FACE",FACE,{"disambiguationData":[OSD([sQuery(id+"F0.wireOp",EDGE,"E0"),subQ0,subQ1,subQ2,subQ3,subQ4,subQ5])],"isStart":false})})});}
            var sketch = newSketch(context, id + "F25", { "sketchPlane" : qUnion([Q0])});
            skCircle(sketch, "E106", {"center": v(-243.07, 12.89) * mm, "radius": 2.7 * mm});
            skCircle(sketch, "E107", {"center": v(-208.05, 12.89) * mm, "radius": 2.7 * mm});
            skCircle(sketch, "E108", {"center": v(-243.07, -11.71) * mm, "radius": 2.7 * mm});
            skCircle(sketch, "E109", {"center": v(-208.05, -11.71) * mm, "radius": 2.7 * mm});
            skCircle(sketch, "E110", {"center": v(-166.77, 24.07) * mm, "radius": 2.7 * mm});
            skCircle(sketch, "E111", {"center": v(-150.74, 28.64) * mm, "radius": 2.7 * mm});
            skCircle(sketch, "E112", {"center": v(-156.42, 18.14) * mm, "radius": 2.7 * mm});
            skCircle(sketch, "E113", {"center": v(-161.16, 34.21) * mm, "radius": 2.7 * mm});
            skCircle(sketch, "E114", {"center": v(-186.57, -38.76) * mm, "radius": 2.7 * mm});
            skCircle(sketch, "E115", {"center": v(-161.15, -39.06) * mm, "radius": 2.7 * mm});
            skCircle(sketch, "E116", {"center": v(-186.53, -78.69) * mm, "radius": 2.7 * mm});
            skCircle(sketch, "E117", {"center": v(-161.56, -78.89) * mm, "radius": 2.7 * mm});
            skCircle(sketch, "E118", {"center": v(-24.95, -46.28) * mm, "radius": 2.7 * mm});
            skCircle(sketch, "E119", {"center": v(-4.53, -46.46) * mm, "radius": 2.7 * mm});
            skCircle(sketch, "E120", {"center": v(-25.1, -81.06) * mm, "radius": 2.7 * mm});
            skCircle(sketch, "E121", {"center": v(-4.92, -81.17) * mm, "radius": 2.7 * mm});
            skCircle(sketch, "E122", {"center": v(-4.53, -46.46) * mm, "radius": 1.33 * mm});
            skCircle(sketch, "E123", {"center": v(-24.95, -46.28) * mm, "radius": 1.33 * mm});
            skCircle(sketch, "E124", {"center": v(-25.1, -81.06) * mm, "radius": 1.33 * mm});
            skCircle(sketch, "E125", {"center": v(-4.95, -81.17) * mm, "radius": 1.33 * mm});
            skCircle(sketch, "E126", {"center": v(-186.57, -38.76) * mm, "radius": 1.33 * mm});
            skCircle(sketch, "E127", {"center": v(-161.15, -39.06) * mm, "radius": 1.33 * mm});
            skCircle(sketch, "E128", {"center": v(-186.53, -78.69) * mm, "radius": 1.33 * mm});
            skCircle(sketch, "E129", {"center": v(-161.56, -78.89) * mm, "radius": 1.33 * mm});
            skCircle(sketch, "E130", {"center": v(-243.07, 12.89) * mm, "radius": 1.33 * mm});
            skCircle(sketch, "E131", {"center": v(-243.07, -11.71) * mm, "radius": 1.33 * mm});
            skCircle(sketch, "E132", {"center": v(-208.05, 12.89) * mm, "radius": 1.33 * mm});
            skCircle(sketch, "E133", {"center": v(-208.05, -11.71) * mm, "radius": 1.33 * mm});
            skCircle(sketch, "E134", {"center": v(-161.16, 34.21) * mm, "radius": 1.33 * mm});
            skCircle(sketch, "E135", {"center": v(-150.74, 28.64) * mm, "radius": 1.33 * mm});
            skCircle(sketch, "E136", {"center": v(-166.77, 24.07) * mm, "radius": 1.33 * mm});
            skCircle(sketch, "E137", {"center": v(-156.42, 18.14) * mm, "radius": 1.33 * mm});
            skSolve(sketch);
        }
        {
            var Q0;
            {var subQ0=sQuery(id+"F0.wireOp",EDGE,"E1");var subQ1=sQuery(id+"F0.wireOp",EDGE,"E2");var subQ2=sQuery(id+"F0.wireOp",EDGE,"E3");var subQ3=sQuery(id+"F0.wireOp",EDGE,"E4");var subQ4=sQuery(id+"F0.wireOp",EDGE,"E5");var subQ5=sQuery(id+"F0.wireOp",EDGE,"E6");var subQ11=makeQuery(id+"F1.opExtrude","SWEPT_FACE",FACE,{"disambiguationData":[OSD([subQ2])]});Q0=makeQuery(id+"F17.boolean.opBoolean","SPLIT",FACE,{"disambiguationData":[TD([subQ11])],"derivedFrom":makeQuery(id+"F16.boolean.opBoolean","SPLIT",FACE,{"disambiguationData":[TD([makeQuery(id+"F1.opExtrude","SWEPT_FACE",FACE,{"disambiguationData":[OSD([subQ1])]})])],"derivedFrom":makeQuery(id+"F1.opExtrude","CAP_FACE",FACE,{"disambiguationData":[OSD([sQuery(id+"F0.wireOp",EDGE,"E0"),subQ0,subQ1,subQ2,subQ3,subQ4,subQ5])],"isStart":false})})});}
            var sketch = newSketch(context, id + "F26", { "sketchPlane" : qUnion([Q0])});
            skCircle(sketch, "E138.cCircle", {"center": v(-242.28, -80.84) * mm, "radius": 7 * mm, "construction": true});
            skLineSegment(sketch, "E138.0", {"start": v(-237.3, -75.93) * mm, "end": v(-235.53, -82.7) * mm});
            skLineSegment(sketch, "E138.1", {"start": v(-235.53, -82.7) * mm, "end": v(-240.52, -87.61) * mm});
            skLineSegment(sketch, "E138.2", {"start": v(-240.52, -87.61) * mm, "end": v(-247.27, -85.75) * mm});
            skLineSegment(sketch, "E138.3", {"start": v(-247.27, -85.75) * mm, "end": v(-249.03, -78.97) * mm});
            skLineSegment(sketch, "E138.4", {"start": v(-249.03, -78.97) * mm, "end": v(-244.04, -74.06) * mm});
            skLineSegment(sketch, "E138.5", {"start": v(-244.04, -74.06) * mm, "end": v(-237.3, -75.93) * mm});
            skCircle(sketch, "E139.cCircle", {"center": v(-37.59, -68.48) * mm, "radius": 7 * mm, "construction": true});
            skLineSegment(sketch, "E139.0", {"start": v(-35.26, -61.88) * mm, "end": v(-30.7, -67.2) * mm});
            skLineSegment(sketch, "E139.1", {"start": v(-30.7, -67.2) * mm, "end": v(-33.03, -73.8) * mm});
            skLineSegment(sketch, "E139.2", {"start": v(-33.03, -73.8) * mm, "end": v(-39.91, -75.08) * mm});
            skLineSegment(sketch, "E139.3", {"start": v(-39.91, -75.08) * mm, "end": v(-44.47, -69.77) * mm});
            skLineSegment(sketch, "E139.4", {"start": v(-44.47, -69.77) * mm, "end": v(-42.14, -63.17) * mm});
            skLineSegment(sketch, "E139.5", {"start": v(-42.14, -63.17) * mm, "end": v(-35.26, -61.88) * mm});
            skCircle(sketch, "E140.cCircle", {"center": v(-190.4, 25.35) * mm, "radius": 7 * mm, "construction": true});
            skLineSegment(sketch, "E140.0", {"start": v(-191.67, 32.23) * mm, "end": v(-185.07, 29.88) * mm});
            skLineSegment(sketch, "E140.1", {"start": v(-185.07, 29.88) * mm, "end": v(-183.8, 23) * mm});
            skLineSegment(sketch, "E140.2", {"start": v(-183.8, 23) * mm, "end": v(-189.14, 18.46) * mm});
            skLineSegment(sketch, "E140.3", {"start": v(-189.14, 18.46) * mm, "end": v(-195.73, 20.81) * mm});
            skLineSegment(sketch, "E140.4", {"start": v(-195.73, 20.81) * mm, "end": v(-197, 27.7) * mm});
            skLineSegment(sketch, "E140.5", {"start": v(-197, 27.7) * mm, "end": v(-191.67, 32.23) * mm});
            skCircle(sketch, "E141.cCircle", {"center": v(-247.33, 145.25) * mm, "radius": 7 * mm, "construction": true});
            skLineSegment(sketch, "E141.0", {"start": v(-246.23, 152.17) * mm, "end": v(-240.8, 147.75) * mm});
            skLineSegment(sketch, "E141.1", {"start": v(-240.8, 147.75) * mm, "end": v(-241.9, 140.84) * mm});
            skLineSegment(sketch, "E141.2", {"start": v(-241.9, 140.84) * mm, "end": v(-248.44, 138.34) * mm});
            skLineSegment(sketch, "E141.3", {"start": v(-248.44, 138.34) * mm, "end": v(-253.87, 142.75) * mm});
            skLineSegment(sketch, "E141.4", {"start": v(-253.87, 142.75) * mm, "end": v(-252.77, 149.67) * mm});
            skLineSegment(sketch, "E141.5", {"start": v(-252.77, 149.67) * mm, "end": v(-246.23, 152.17) * mm});
            skCircle(sketch, "E142.cCircle", {"center": v(129.83, -85.79) * mm, "radius": 7 * mm, "construction": true});
            skLineSegment(sketch, "E142.0", {"start": v(133.21, -79.66) * mm, "end": v(136.82, -85.66) * mm});
            skLineSegment(sketch, "E142.1", {"start": v(136.82, -85.66) * mm, "end": v(133.43, -91.78) * mm});
            skLineSegment(sketch, "E142.2", {"start": v(133.43, -91.78) * mm, "end": v(126.44, -91.91) * mm});
            skLineSegment(sketch, "E142.3", {"start": v(126.44, -91.91) * mm, "end": v(122.83, -85.91) * mm});
            skLineSegment(sketch, "E142.4", {"start": v(122.83, -85.91) * mm, "end": v(126.22, -79.79) * mm});
            skLineSegment(sketch, "E142.5", {"start": v(126.22, -79.79) * mm, "end": v(133.21, -79.66) * mm});
            skSolve(sketch);
        }
        {
            var Q0;
            Q0=makeQuery(id+"F26.imprint","IMPRINT",FACE,{"disambiguationData":[TD([[makeQuery(id+"F26.imprint","IMPRINT",EDGE,{"derivedFrom":sQuery(id+"F26.wireOp",EDGE,"E141.0")}),-1.0]])]});
            var Q1;
            Q1=makeQuery(id+"F26.imprint","IMPRINT",FACE,{"disambiguationData":[TD([[makeQuery(id+"F26.imprint","IMPRINT",EDGE,{"derivedFrom":sQuery(id+"F26.wireOp",EDGE,"E140.0")}),-1.0]])]});
            var Q2;
            Q2=makeQuery(id+"F26.imprint","IMPRINT",FACE,{"disambiguationData":[TD([[makeQuery(id+"F26.imprint","IMPRINT",EDGE,{"derivedFrom":sQuery(id+"F26.wireOp",EDGE,"E139.0")}),-1.0]])]});
            var Q3;
            Q3=makeQuery(id+"F26.imprint","IMPRINT",FACE,{"disambiguationData":[TD([[makeQuery(id+"F26.imprint","IMPRINT",EDGE,{"derivedFrom":sQuery(id+"F26.wireOp",EDGE,"E138.0")}),-1.0]])]});
            var Q4;
            Q4=makeQuery(id+"F26.imprint","IMPRINT",FACE,{"disambiguationData":[TD([[makeQuery(id+"F26.imprint","IMPRINT",EDGE,{"derivedFrom":sQuery(id+"F26.wireOp",EDGE,"E142.0")}),-1.0]])]});
            extrude(context, id + "F27", {"entities" : qUnion([Q0, Q1, Q2, Q3, Q4]), "operationType" : NewBodyOperationType.REMOVE, "oppositeDirection" : true, "depth" : 6.9 * mm});
        }
        {
            var Q0;
            Q0=makeQuery(id+"F25.imprint","IMPRINT",FACE,{"disambiguationData":[TD([[makeQuery(id+"F25.imprint","IMPRINT",EDGE,{"derivedFrom":sQuery(id+"F25.wireOp",EDGE,"E121")}),1.0]])]});
            var Q1;
            Q1=makeQuery(id+"F25.imprint","IMPRINT",FACE,{"disambiguationData":[TD([[makeQuery(id+"F25.imprint","IMPRINT",EDGE,{"derivedFrom":sQuery(id+"F25.wireOp",EDGE,"E118")}),1.0]])]});
            var Q2;
            Q2=makeQuery(id+"F25.imprint","IMPRINT",FACE,{"disambiguationData":[TD([[makeQuery(id+"F25.imprint","IMPRINT",EDGE,{"derivedFrom":sQuery(id+"F25.wireOp",EDGE,"E109")}),1.0]])]});
            var Q3;
            Q3=makeQuery(id+"F25.imprint","IMPRINT",FACE,{"disambiguationData":[TD([[makeQuery(id+"F25.imprint","IMPRINT",EDGE,{"derivedFrom":sQuery(id+"F25.wireOp",EDGE,"E111")}),1.0]])]});
            var Q4;
            Q4=makeQuery(id+"F25.imprint","IMPRINT",FACE,{"disambiguationData":[TD([[makeQuery(id+"F25.imprint","IMPRINT",EDGE,{"derivedFrom":sQuery(id+"F25.wireOp",EDGE,"E120")}),1.0]])]});
            var Q5;
            Q5=makeQuery(id+"F25.imprint","IMPRINT",FACE,{"disambiguationData":[TD([[makeQuery(id+"F25.imprint","IMPRINT",EDGE,{"derivedFrom":sQuery(id+"F25.wireOp",EDGE,"E116")}),1.0]])]});
            var Q6;
            Q6=makeQuery(id+"F25.imprint","IMPRINT",FACE,{"disambiguationData":[TD([[makeQuery(id+"F25.imprint","IMPRINT",EDGE,{"derivedFrom":sQuery(id+"F25.wireOp",EDGE,"E115")}),1.0]])]});
            var Q7;
            Q7=makeQuery(id+"F25.imprint","IMPRINT",FACE,{"disambiguationData":[TD([[makeQuery(id+"F25.imprint","IMPRINT",EDGE,{"derivedFrom":sQuery(id+"F25.wireOp",EDGE,"E114")}),1.0]])]});
            var Q8;
            Q8=makeQuery(id+"F25.imprint","IMPRINT",FACE,{"disambiguationData":[TD([[makeQuery(id+"F25.imprint","IMPRINT",EDGE,{"derivedFrom":sQuery(id+"F25.wireOp",EDGE,"E107")}),1.0]])]});
            var Q9;
            Q9=makeQuery(id+"F25.imprint","IMPRINT",FACE,{"disambiguationData":[TD([[makeQuery(id+"F25.imprint","IMPRINT",EDGE,{"derivedFrom":sQuery(id+"F25.wireOp",EDGE,"E112")}),1.0]])]});
            var Q10;
            Q10=makeQuery(id+"F25.imprint","IMPRINT",FACE,{"disambiguationData":[TD([[makeQuery(id+"F25.imprint","IMPRINT",EDGE,{"derivedFrom":sQuery(id+"F25.wireOp",EDGE,"E106")}),1.0]])]});
            var Q11;
            Q11=makeQuery(id+"F25.imprint","IMPRINT",FACE,{"disambiguationData":[TD([[makeQuery(id+"F25.imprint","IMPRINT",EDGE,{"derivedFrom":sQuery(id+"F25.wireOp",EDGE,"E117")}),1.0]])]});
            var Q12;
            Q12=makeQuery(id+"F25.imprint","IMPRINT",FACE,{"disambiguationData":[TD([[makeQuery(id+"F25.imprint","IMPRINT",EDGE,{"derivedFrom":sQuery(id+"F25.wireOp",EDGE,"E113")}),1.0]])]});
            var Q13;
            Q13=makeQuery(id+"F25.imprint","IMPRINT",FACE,{"disambiguationData":[TD([[makeQuery(id+"F25.imprint","IMPRINT",EDGE,{"derivedFrom":sQuery(id+"F25.wireOp",EDGE,"E119")}),1.0]])]});
            var Q14;
            Q14=makeQuery(id+"F25.imprint","IMPRINT",FACE,{"disambiguationData":[TD([[makeQuery(id+"F25.imprint","IMPRINT",EDGE,{"derivedFrom":sQuery(id+"F25.wireOp",EDGE,"E110")}),1.0]])]});
            var Q15;
            Q15=makeQuery(id+"F25.imprint","IMPRINT",FACE,{"disambiguationData":[TD([[makeQuery(id+"F25.imprint","IMPRINT",EDGE,{"derivedFrom":sQuery(id+"F25.wireOp",EDGE,"E108")}),1.0]])]});
            extrude(context, id + "F28", {"entities" : qUnion([Q0, Q1, Q2, Q3, Q4, Q5, Q6, Q7, Q8, Q9, Q10, Q11, Q12, Q13, Q14, Q15]), "operationType" : NewBodyOperationType.REMOVE, "oppositeDirection" : true, "depth" : 2.3 * mm});
        }
        {
            var Q0;
            Q0=makeQuery(id+"F25.imprint","IMPRINT",FACE,{"disambiguationData":[TD([[makeQuery(id+"F25.imprint","IMPRINT",EDGE,{"derivedFrom":sQuery(id+"F25.wireOp",EDGE,"E135")}),1.0]])]});
            var Q1;
            Q1=makeQuery(id+"F25.imprint","IMPRINT",FACE,{"disambiguationData":[TD([[makeQuery(id+"F25.imprint","IMPRINT",EDGE,{"derivedFrom":sQuery(id+"F25.wireOp",EDGE,"E128")}),1.0]])]});
            var Q2;
            Q2=makeQuery(id+"F25.imprint","IMPRINT",FACE,{"disambiguationData":[TD([[makeQuery(id+"F25.imprint","IMPRINT",EDGE,{"derivedFrom":sQuery(id+"F25.wireOp",EDGE,"E132")}),1.0]])]});
            var Q3;
            Q3=makeQuery(id+"F25.imprint","IMPRINT",FACE,{"disambiguationData":[TD([[makeQuery(id+"F25.imprint","IMPRINT",EDGE,{"derivedFrom":sQuery(id+"F25.wireOp",EDGE,"E127")}),1.0]])]});
            var Q4;
            Q4=makeQuery(id+"F25.imprint","IMPRINT",FACE,{"disambiguationData":[TD([[makeQuery(id+"F25.imprint","IMPRINT",EDGE,{"derivedFrom":sQuery(id+"F25.wireOp",EDGE,"E133")}),1.0]])]});
            var Q5;
            Q5=makeQuery(id+"F25.imprint","IMPRINT",FACE,{"disambiguationData":[TD([[makeQuery(id+"F25.imprint","IMPRINT",EDGE,{"derivedFrom":sQuery(id+"F25.wireOp",EDGE,"E129")}),1.0]])]});
            var Q6;
            Q6=makeQuery(id+"F25.imprint","IMPRINT",FACE,{"disambiguationData":[TD([[makeQuery(id+"F25.imprint","IMPRINT",EDGE,{"derivedFrom":sQuery(id+"F25.wireOp",EDGE,"E123")}),1.0]])]});
            var Q7;
            Q7=makeQuery(id+"F25.imprint","IMPRINT",FACE,{"disambiguationData":[TD([[makeQuery(id+"F25.imprint","IMPRINT",EDGE,{"derivedFrom":sQuery(id+"F25.wireOp",EDGE,"E125")}),1.0]])]});
            var Q8;
            Q8=makeQuery(id+"F25.imprint","IMPRINT",FACE,{"disambiguationData":[TD([[makeQuery(id+"F25.imprint","IMPRINT",EDGE,{"derivedFrom":sQuery(id+"F25.wireOp",EDGE,"E131")}),1.0]])]});
            var Q9;
            Q9=makeQuery(id+"F25.imprint","IMPRINT",FACE,{"disambiguationData":[TD([[makeQuery(id+"F25.imprint","IMPRINT",EDGE,{"derivedFrom":sQuery(id+"F25.wireOp",EDGE,"E137")}),1.0]])]});
            var Q10;
            Q10=makeQuery(id+"F25.imprint","IMPRINT",FACE,{"disambiguationData":[TD([[makeQuery(id+"F25.imprint","IMPRINT",EDGE,{"derivedFrom":sQuery(id+"F25.wireOp",EDGE,"E122")}),1.0]])]});
            var Q11;
            Q11=makeQuery(id+"F25.imprint","IMPRINT",FACE,{"disambiguationData":[TD([[makeQuery(id+"F25.imprint","IMPRINT",EDGE,{"derivedFrom":sQuery(id+"F25.wireOp",EDGE,"E126")}),1.0]])]});
            var Q12;
            Q12=makeQuery(id+"F25.imprint","IMPRINT",FACE,{"disambiguationData":[TD([[makeQuery(id+"F25.imprint","IMPRINT",EDGE,{"derivedFrom":sQuery(id+"F25.wireOp",EDGE,"E136")}),1.0]])]});
            var Q13;
            Q13=makeQuery(id+"F25.imprint","IMPRINT",FACE,{"disambiguationData":[TD([[makeQuery(id+"F25.imprint","IMPRINT",EDGE,{"derivedFrom":sQuery(id+"F25.wireOp",EDGE,"E130")}),1.0]])]});
            var Q14;
            Q14=makeQuery(id+"F25.imprint","IMPRINT",FACE,{"disambiguationData":[TD([[makeQuery(id+"F25.imprint","IMPRINT",EDGE,{"derivedFrom":sQuery(id+"F25.wireOp",EDGE,"E134")}),1.0]])]});
            var Q15;
            Q15=makeQuery(id+"F25.imprint","IMPRINT",FACE,{"disambiguationData":[TD([[makeQuery(id+"F25.imprint","IMPRINT",EDGE,{"derivedFrom":sQuery(id+"F25.wireOp",EDGE,"E124")}),1.0]])]});
            extrude(context, id + "F29", {"entities" : qUnion([Q0, Q1, Q2, Q3, Q4, Q5, Q6, Q7, Q8, Q9, Q10, Q11, Q12, Q13, Q14, Q15]), "operationType" : NewBodyOperationType.REMOVE, "oppositeDirection" : true, "depth" : 30 * mm});
        }
        {
            var Q0;
            {var subQ0=sQuery(id+"F0.wireOp",EDGE,"E1");var subQ1=sQuery(id+"F0.wireOp",EDGE,"E2");var subQ2=sQuery(id+"F0.wireOp",EDGE,"E3");var subQ3=sQuery(id+"F0.wireOp",EDGE,"E4");var subQ4=sQuery(id+"F0.wireOp",EDGE,"E5");var subQ5=sQuery(id+"F0.wireOp",EDGE,"E6");var subQ7=makeQuery(id+"F1.opExtrude","SWEPT_FACE",FACE,{"disambiguationData":[OSD([subQ1])]});Q0=makeQuery(id+"F17.boolean.opBoolean","SPLIT",FACE,{"disambiguationData":[TD([subQ7])],"derivedFrom":makeQuery(id+"F16.boolean.opBoolean","SPLIT",FACE,{"disambiguationData":[TD([subQ7])],"derivedFrom":makeQuery(id+"F1.opExtrude","CAP_FACE",FACE,{"disambiguationData":[OSD([sQuery(id+"F0.wireOp",EDGE,"E0"),subQ0,subQ1,subQ2,subQ3,subQ4,subQ5])],"isStart":true})})});}
            var sketch = newSketch(context, id + "F30", { "sketchPlane" : qUnion([Q0])});
            skLineSegment(sketch, "E143", {"start": v(-117.68, -87.63) * mm, "end": v(-12.15, -87.63) * mm});
            skLineSegment(sketch, "E144", {"start": v(-12.15, -87.63) * mm, "end": v(-12.15, -66.82) * mm});
            skLineSegment(sketch, "E145", {"start": v(-12.15, -66.82) * mm, "end": v(-117.68, -80.02) * mm});
            skLineSegment(sketch, "E146", {"start": v(-117.68, -80.02) * mm, "end": v(-117.68, -87.63) * mm});
            skLineSegment(sketch, "E147", {"start": v(48.66, -50.17) * mm, "end": v(48.66, -87.63) * mm});
            skLineSegment(sketch, "E148", {"start": v(48.66, -87.63) * mm, "end": v(149.44, -87.63) * mm});
            skLineSegment(sketch, "E149", {"start": v(149.44, -87.63) * mm, "end": v(149.44, 8.62) * mm});
            skLineSegment(sketch, "E150", {"start": v(48.66, -50.17) * mm, "end": v(149.44, 8.62) * mm});
            skLineSegment(sketch, "E151.bottom", {"start": v(199.13, -86.86) * mm, "end": v(231.58, -86.86) * mm});
            skLineSegment(sketch, "E151.top", {"start": v(199.13, -24.66) * mm, "end": v(231.58, -24.66) * mm});
            skLineSegment(sketch, "E151.left", {"start": v(199.13, -86.86) * mm, "end": v(199.13, -24.66) * mm});
            skLineSegment(sketch, "E151.right", {"start": v(231.58, -86.86) * mm, "end": v(231.58, -24.66) * mm});
            skLineSegment(sketch, "E152", {"start": v(184.51, 43.8) * mm, "end": v(249.09, 125.82) * mm});
            skLineSegment(sketch, "E153", {"start": v(249.09, 125.82) * mm, "end": v(249.09, 25.75) * mm});
            skLineSegment(sketch, "E154", {"start": v(249.09, 25.75) * mm, "end": v(184.51, 43.8) * mm});
            skSolve(sketch);
        }
        {
            var Q0;
            Q0=makeQuery(id+"F30.imprint","IMPRINT",FACE,{"disambiguationData":[TD([[makeQuery(id+"F30.imprint","IMPRINT",EDGE,{"derivedFrom":sQuery(id+"F30.wireOp",EDGE,"E147")}),1.0]])]});
            var Q1;
            Q1=makeQuery(id+"F30.imprint","IMPRINT",FACE,{"disambiguationData":[TD([[makeQuery(id+"F30.imprint","IMPRINT",EDGE,{"derivedFrom":sQuery(id+"F30.wireOp",EDGE,"E151.bottom")}),1.0]])]});
            var Q2;
            Q2=makeQuery(id+"F30.imprint","IMPRINT",FACE,{"disambiguationData":[TD([[makeQuery(id+"F30.imprint","IMPRINT",EDGE,{"derivedFrom":sQuery(id+"F30.wireOp",EDGE,"E152")}),-1.0]])]});
            var Q3;
            Q3=makeQuery(id+"F30.imprint","IMPRINT",FACE,{"disambiguationData":[TD([[makeQuery(id+"F30.imprint","IMPRINT",EDGE,{"derivedFrom":sQuery(id+"F30.wireOp",EDGE,"E143")}),1.0]])]});
            extrude(context, id + "F31", {"entities" : qUnion([Q0, Q1, Q2, Q3]), "operationType" : NewBodyOperationType.REMOVE, "oppositeDirection" : true, "depth" : 30 * mm});
        }
        {
            var Q0;
            {var subQ0=sQuery(id+"F0.wireOp",EDGE,"E0");var subQ1=sQuery(id+"F0.wireOp",EDGE,"E1");var subQ2=sQuery(id+"F0.wireOp",EDGE,"E6");Q0=makeQuery(id+"F16.boolean.opBoolean","SPLIT",FACE,{"disambiguationData":[TD([makeQuery(id+"F1.opExtrude","SWEPT_FACE",FACE,{"disambiguationData":[OSD([subQ0])]})])],"derivedFrom":makeQuery(id+"F1.opExtrude","CAP_FACE",FACE,{"disambiguationData":[OSD([subQ0,subQ1,sQuery(id+"F0.wireOp",EDGE,"E2"),sQuery(id+"F0.wireOp",EDGE,"E3"),sQuery(id+"F0.wireOp",EDGE,"E4"),sQuery(id+"F0.wireOp",EDGE,"E5"),subQ2])],"isStart":true})});}
            shell(context, id + "F32", {"entities" : qUnion([Q0]), "thickness" : 3 * mm});
        }
        {
            var Q0;
            {var subQ0=sQuery(id+"F0.wireOp",EDGE,"E1");var subQ1=sQuery(id+"F0.wireOp",EDGE,"E2");var subQ2=sQuery(id+"F0.wireOp",EDGE,"E3");var subQ3=sQuery(id+"F0.wireOp",EDGE,"E4");var subQ4=sQuery(id+"F0.wireOp",EDGE,"E5");var subQ5=sQuery(id+"F0.wireOp",EDGE,"E6");var subQ7=makeQuery(id+"F1.opExtrude","SWEPT_FACE",FACE,{"disambiguationData":[OSD([subQ1])]});Q0=makeQuery(id+"F17.boolean.opBoolean","SPLIT",FACE,{"disambiguationData":[TD([subQ7])],"derivedFrom":makeQuery(id+"F16.boolean.opBoolean","SPLIT",FACE,{"disambiguationData":[TD([subQ7])],"derivedFrom":makeQuery(id+"F1.opExtrude","CAP_FACE",FACE,{"disambiguationData":[OSD([sQuery(id+"F0.wireOp",EDGE,"E0"),subQ0,subQ1,subQ2,subQ3,subQ4,subQ5])],"isStart":true})})});}
            shell(context, id + "F33", {"entities" : qUnion([Q0]), "thickness" : 3 * mm});
        }
        {
            var Q0;
            {var subQ0=sQuery(id+"F0.wireOp",EDGE,"E1");var subQ1=sQuery(id+"F0.wireOp",EDGE,"E2");var subQ2=sQuery(id+"F0.wireOp",EDGE,"E3");var subQ3=sQuery(id+"F0.wireOp",EDGE,"E4");var subQ4=sQuery(id+"F0.wireOp",EDGE,"E5");var subQ5=sQuery(id+"F0.wireOp",EDGE,"E6");var subQ9=makeQuery(id+"F9.boolean.opBoolean","COPY",FACE,{"derivedFrom":makeQuery(id+"F9.opExtrude","SWEPT_FACE",FACE,{"disambiguationData":[OSD([sQuery(id+"F8.wireOp",EDGE,"E16.0")])]})});Q0=makeQuery(id+"F17.boolean.opBoolean","SPLIT",FACE,{"disambiguationData":[TD([subQ9])],"derivedFrom":makeQuery(id+"F16.boolean.opBoolean","SPLIT",FACE,{"disambiguationData":[TD([makeQuery(id+"F1.opExtrude","SWEPT_FACE",FACE,{"disambiguationData":[OSD([subQ1])]})])],"derivedFrom":makeQuery(id+"F1.opExtrude","CAP_FACE",FACE,{"disambiguationData":[OSD([sQuery(id+"F0.wireOp",EDGE,"E0"),subQ0,subQ1,subQ2,subQ3,subQ4,subQ5])],"isStart":true})})});}
            shell(context, id + "F34", {"entities" : qUnion([Q0]), "thickness" : 2.5 * mm});
        }
        {
            var Q0;
            {var subQ0=sQuery(id+"F0.wireOp",EDGE,"E1");var subQ1=sQuery(id+"F0.wireOp",EDGE,"E2");var subQ2=sQuery(id+"F0.wireOp",EDGE,"E3");var subQ3=sQuery(id+"F0.wireOp",EDGE,"E4");var subQ4=sQuery(id+"F0.wireOp",EDGE,"E5");var subQ5=sQuery(id+"F0.wireOp",EDGE,"E6");var subQ18=makeQuery(id+"F1.opExtrude","SWEPT_FACE",FACE,{"disambiguationData":[OSD([subQ2])]});Q0=makeQuery(id+"F17.boolean.opBoolean","SPLIT",FACE,{"disambiguationData":[TD([subQ18])],"derivedFrom":makeQuery(id+"F16.boolean.opBoolean","SPLIT",FACE,{"disambiguationData":[TD([makeQuery(id+"F1.opExtrude","SWEPT_FACE",FACE,{"disambiguationData":[OSD([subQ1])]})])],"derivedFrom":makeQuery(id+"F1.opExtrude","CAP_FACE",FACE,{"disambiguationData":[OSD([sQuery(id+"F0.wireOp",EDGE,"E0"),subQ0,subQ1,subQ2,subQ3,subQ4,subQ5])],"isStart":true})})});}
            shell(context, id + "F35", {"entities" : qUnion([Q0]), "thickness" : 2.75 * mm});
        }
        {
            var Q0;
            Q0=qCreatedBy(makeId("Front.planeOp"),FACE);
            cPlane(context, id + "F36", {"entities" : qUnion([Q0]), "cplaneType" : CPlaneType.OFFSET, "offset" : 150 * mm, "width" : 150 * mm, "height" : 150 * mm});
        }
        {
            var Q0;
            Q0=qCreatedBy(makeId("Front.planeOp"),FACE);
            var sketch = newSketch(context, id + "F37", { "sketchPlane" : qUnion([Q0])});
            skLineSegment(sketch, "E155.bottom", {"start": v(329.39, 200.06) * mm, "end": v(-148.5, 200.06) * mm});
            skLineSegment(sketch, "E155.top", {"start": v(329.39, -147.7) * mm, "end": v(-148.5, -147.7) * mm});
            skLineSegment(sketch, "E155.left", {"start": v(329.39, 200.06) * mm, "end": v(329.39, -147.7) * mm});
            skLineSegment(sketch, "E155.right", {"start": v(-148.5, 200.06) * mm, "end": v(-148.5, -147.7) * mm});
            skSolve(sketch);
        }
        {
            var Q0;
            Q0=makeQuery(id+"F37.imprint","IMPRINT",FACE,{"disambiguationData":[TD([[makeQuery(id+"F37.imprint","IMPRINT",EDGE,{"derivedFrom":sQuery(id+"F37.wireOp",EDGE,"E155.bottom")}),1.0]])]});
            extrude(context, id + "F38", {"entities" : qUnion([Q0]), "operationType" : NewBodyOperationType.REMOVE, "oppositeDirection" : true, "depth" : 5.7 * mm});
        }
        {
            var Q0;
            Q0=makeQuery(id+"F16.boolean.opBoolean","SPLIT",BODY,{"disambiguationData":[OD(1.0)],"derivedFrom":makeQuery(id+"F1.opExtrude","SWEPT_BODY",BODY,{"disambiguationData":[OSD([sQuery(id+"F0.wireOp",EDGE,"E0"),sQuery(id+"F0.wireOp",EDGE,"E1"),sQuery(id+"F0.wireOp",EDGE,"E2"),sQuery(id+"F0.wireOp",EDGE,"E3"),sQuery(id+"F0.wireOp",EDGE,"E4"),sQuery(id+"F0.wireOp",EDGE,"E5"),sQuery(id+"F0.wireOp",EDGE,"E6")])]})});
            var Q1;
            Q1=makeQuery(id+"F17.boolean.opBoolean","SPLIT",BODY,{"disambiguationData":[OD(0.0)],"derivedFrom":makeQuery(id+"F16.boolean.opBoolean","SPLIT",BODY,{"disambiguationData":[OD(0.0)],"derivedFrom":makeQuery(id+"F1.opExtrude","SWEPT_BODY",BODY,{"disambiguationData":[OSD([sQuery(id+"F0.wireOp",EDGE,"E0"),sQuery(id+"F0.wireOp",EDGE,"E1"),sQuery(id+"F0.wireOp",EDGE,"E2"),sQuery(id+"F0.wireOp",EDGE,"E3"),sQuery(id+"F0.wireOp",EDGE,"E4"),sQuery(id+"F0.wireOp",EDGE,"E5"),sQuery(id+"F0.wireOp",EDGE,"E6")])]})})});
            var Q2;
            Q2=makeQuery(id+"F17.boolean.opBoolean","SPLIT",BODY,{"disambiguationData":[OD(1.0)],"derivedFrom":makeQuery(id+"F16.boolean.opBoolean","SPLIT",BODY,{"disambiguationData":[OD(0.0)],"derivedFrom":makeQuery(id+"F1.opExtrude","SWEPT_BODY",BODY,{"disambiguationData":[OSD([sQuery(id+"F0.wireOp",EDGE,"E0"),sQuery(id+"F0.wireOp",EDGE,"E1"),sQuery(id+"F0.wireOp",EDGE,"E2"),sQuery(id+"F0.wireOp",EDGE,"E3"),sQuery(id+"F0.wireOp",EDGE,"E4"),sQuery(id+"F0.wireOp",EDGE,"E5"),sQuery(id+"F0.wireOp",EDGE,"E6")])]})})});
            var Q3;
            Q3=makeQuery(id+"F17.boolean.opBoolean","SPLIT",BODY,{"disambiguationData":[OD(2.0)],"derivedFrom":makeQuery(id+"F16.boolean.opBoolean","SPLIT",BODY,{"disambiguationData":[OD(0.0)],"derivedFrom":makeQuery(id+"F1.opExtrude","SWEPT_BODY",BODY,{"disambiguationData":[OSD([sQuery(id+"F0.wireOp",EDGE,"E0"),sQuery(id+"F0.wireOp",EDGE,"E1"),sQuery(id+"F0.wireOp",EDGE,"E2"),sQuery(id+"F0.wireOp",EDGE,"E3"),sQuery(id+"F0.wireOp",EDGE,"E4"),sQuery(id+"F0.wireOp",EDGE,"E5"),sQuery(id+"F0.wireOp",EDGE,"E6")])]})})});
            var Q4;
            Q4=makeQuery(id+"F24.opExtrude","SWEPT_BODY",BODY,{"disambiguationData":[OSD([sQuery(id+"F23.wireOp",EDGE,"E98.0"),sQuery(id+"F23.wireOp",EDGE,"E98.1"),sQuery(id+"F23.wireOp",EDGE,"E98.2"),sQuery(id+"F23.wireOp",EDGE,"E98.3"),sQuery(id+"F23.wireOp",EDGE,"E98.4"),sQuery(id+"F23.wireOp",EDGE,"E98.5"),sQuery(id+"F23.wireOp",EDGE,"E98.6"),sQuery(id+"F23.wireOp",EDGE,"E98.7")])]});
            var Q5;
            Q5=makeQuery(id+"F24.opExtrude","SWEPT_BODY",BODY,{"disambiguationData":[OSD([sQuery(id+"F23.wireOp",EDGE,"E99.0"),sQuery(id+"F23.wireOp",EDGE,"E99.1"),sQuery(id+"F23.wireOp",EDGE,"E99.2"),sQuery(id+"F23.wireOp",EDGE,"E99.3"),sQuery(id+"F23.wireOp",EDGE,"E102.filletArc"),sQuery(id+"F23.wireOp",EDGE,"E103.filletArc"),sQuery(id+"F23.wireOp",EDGE,"E104.filletArc"),sQuery(id+"F23.wireOp",EDGE,"E105.filletArc")])]});
            var Q6;
            Q6=makeQuery(id+"F24.opExtrude","SWEPT_BODY",BODY,{"disambiguationData":[OSD([sQuery(id+"F23.wireOp",EDGE,"E100.0"),sQuery(id+"F23.wireOp",EDGE,"E100.1"),sQuery(id+"F23.wireOp",EDGE,"E100.2"),sQuery(id+"F23.wireOp",EDGE,"E100.3"),sQuery(id+"F23.wireOp",EDGE,"E100.4"),sQuery(id+"F23.wireOp",EDGE,"E100.5"),sQuery(id+"F23.wireOp",EDGE,"E100.6"),sQuery(id+"F23.wireOp",EDGE,"E100.7")])]});
            var Q7;
            Q7=makeQuery(id+"F24.opExtrude","SWEPT_BODY",BODY,{"disambiguationData":[OSD([sQuery(id+"F23.wireOp",EDGE,"E101.0"),sQuery(id+"F23.wireOp",EDGE,"E101.1"),sQuery(id+"F23.wireOp",EDGE,"E101.2"),sQuery(id+"F23.wireOp",EDGE,"E101.3"),sQuery(id+"F23.wireOp",EDGE,"E101.4"),sQuery(id+"F23.wireOp",EDGE,"E101.5"),sQuery(id+"F23.wireOp",EDGE,"E101.6"),sQuery(id+"F23.wireOp",EDGE,"E101.7")])]});
            var Q8;
            Q8=qCreatedBy(id+"F36.planeOp",FACE);
            mirror(context, id + "F39", {"entities" : qUnion([Q0, Q1, Q2, Q3, Q4, Q5, Q6, Q7]), "mirrorPlane" : qUnion([Q8])});
        }
    });
